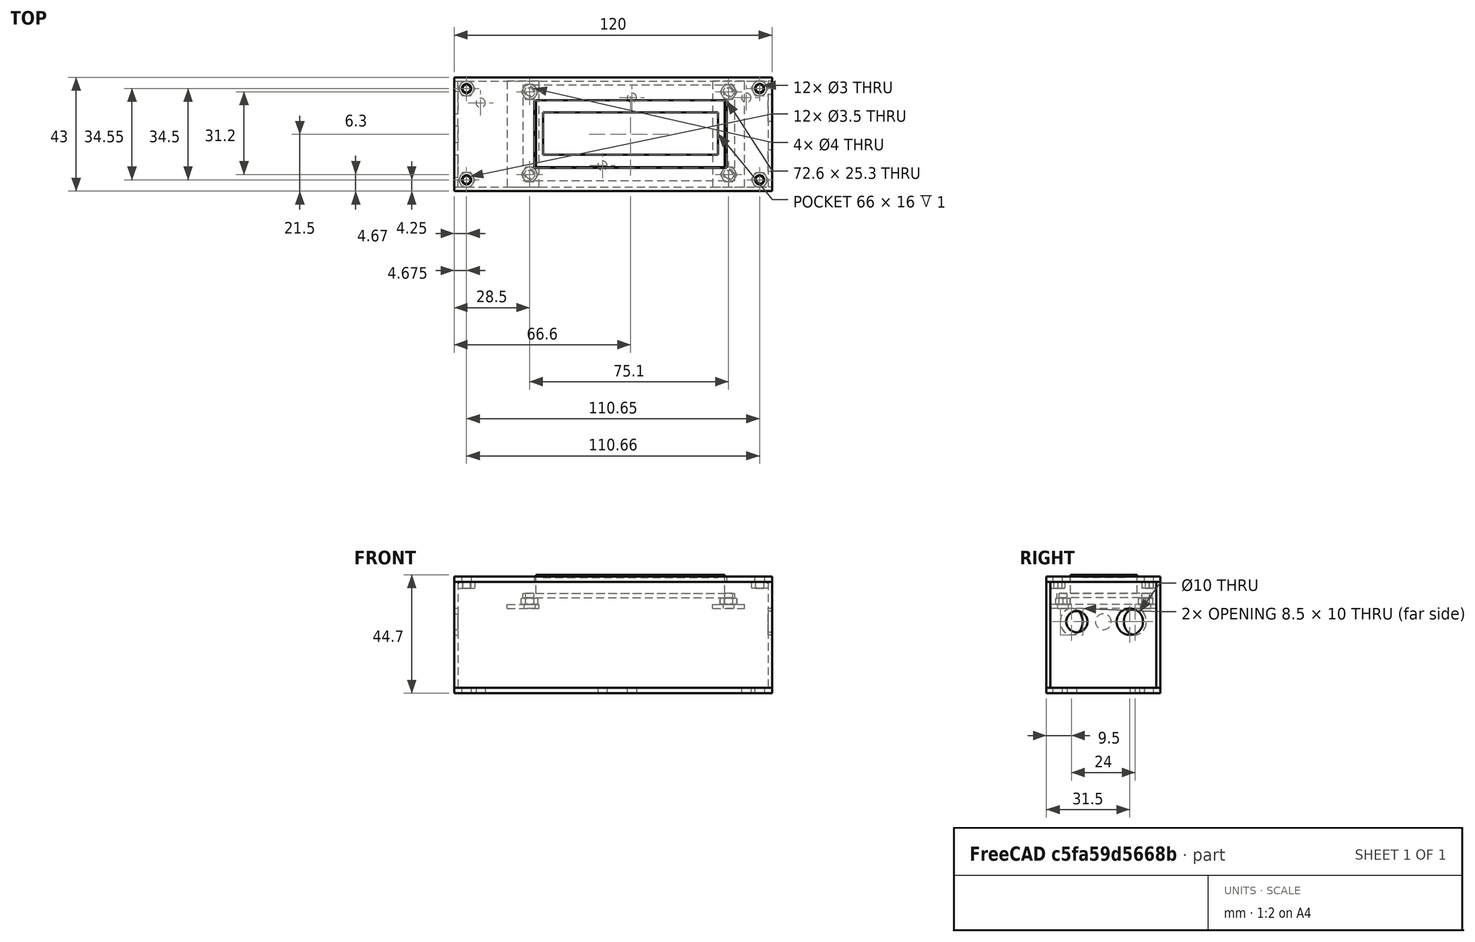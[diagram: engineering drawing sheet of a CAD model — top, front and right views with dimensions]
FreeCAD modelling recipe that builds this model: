
FCSTD DOCUMENT  (FreeCAD 0.19R24291 (Git))
Label: lc_meter_frame
License: All rights reserved
LicenseURL: http://en.wikipedia.org/wiki/All_rights_reserved
objects: TechDraw::DrawViewDimension×49, Sketcher::SketchObject×40, PartDesign::Pad×15, PartDesign::Pocket×14, PartDesign::Body×14, TechDraw::DrawViewPart×9, PartDesign::Mirrored×7, Part::Mirroring×7, TechDraw::DrawViewAnnotation×6, PartDesign::Groove×5, TechDraw::DrawSVGTemplate×4, TechDraw::DrawPage×4, App::Part×3, PartDesign::Plane×2, TechDraw::DrawViewDimExtent×2, TechDraw::DrawViewSection×2, PartDesign::Hole×1, TechDraw::DrawViewBalloon×1
note: 140 computed .brp shape members not serialized (recipe doc carries the construction recipe); baked Part::Feature solids carry a one-line shape summary decoded from their .brp

FEATURE [Sketcher::SketchObject] Sketch007
  FullyConstrained = true
  MapMode = 5
  Support = -> [XY_Plane006]
  sketch-geometry (7):
    g0: LineSegment StartX=1.58771 StartY=2.75 StartZ=0 EndX=-1.58771 EndY=2.75 EndZ=0
    g1: LineSegment StartX=-1.58771 StartY=2.75 StartZ=0 EndX=-3.17543 EndY=1.48956e-11 EndZ=0
    g2: LineSegment StartX=-3.17543 StartY=1.48956e-11 StartZ=0 EndX=-1.58771 EndY=-2.75 EndZ=0
    g3: LineSegment StartX=-1.58771 StartY=-2.75 StartZ=0 EndX=1.58771 EndY=-2.75 EndZ=0
    g4: LineSegment StartX=1.58771 StartY=-2.75 StartZ=0 EndX=3.17543 EndY=2.08953e-11 EndZ=0
    g5: LineSegment StartX=3.17543 StartY=2.08953e-11 StartZ=0 EndX=1.58771 EndY=2.75 EndZ=0
    g6: Circle CenterX=0 CenterY=0 CenterZ=0 NormalX=0 NormalY=0 NormalZ=1 AngleXU=0 Radius=3.17543
  constraints (16):
    c: Coincident(g0,g1)
    c: Coincident(g1,g2)
    c: Coincident(g2,g3)
    c: Coincident(g3,g4)
    c: Coincident(g4,g5)
    c: Coincident(g5,g0)
    c: Equal(g0, g1-g5) x5
    c: PointOnObject(g0,g6)
    c: PointOnObject(g1,g6)
    c: PointOnObject(g2,g6)
    c: PointOnObject(g3,g6)
    c: PointOnObject(g4,g6)
    c: PointOnObject(g5,g6)
    c: Coincident(g6,g-1)
    c: Horizontal(g0)
    c: Distance(g0,g3) = 5.5
FEATURE [PartDesign::Pad] Pad005
  Direction = (1,1,1)
  Length = 1.2
  Length2 = 1.2
  Profile = -> Sketch007
  Type = 4
FEATURE [Sketcher::SketchObject] Sketch008
  FullyConstrained = true
  MapMode = 5
  Placement = pos=(0,0,1.2) rot=(0,0,1;0rad)
  Support = -> [Pad005]
  sketch-geometry (1):
    g0: Circle CenterX=0 CenterY=0 CenterZ=0 NormalX=0 NormalY=0 NormalZ=1 AngleXU=0 Radius=1.5
  constraints (2):
    c: Coincident(g0,g-1)
    c: Diameter(g0) = 3
FEATURE [PartDesign::Pocket] Pocket002
  BaseFeature = -> Pad005
  Length = 5
  Length2 = 100
  Profile = -> Sketch008
  Type = 1
FEATURE [Sketcher::SketchObject] Sketch009
  ExternalGeometry = -> [Pocket002]
  FullyConstrained = true
  MapMode = 5
  Placement = pos=(0,2.75,0) rot=(0,0.707107,0.707107;3.14159rad)
  Support = -> [Pocket002]
  sketch-geometry (3):
    g0: LineSegment StartX=2.5 StartY=1.2 StartZ=0 EndX=3.17543 EndY=0.810042 EndZ=0
    g1: LineSegment StartX=3.17543 StartY=0.810042 StartZ=0 EndX=3.17543 EndY=1.2 EndZ=0
    g2: LineSegment StartX=3.17543 StartY=1.2 StartZ=0 EndX=2.5 EndY=1.2 EndZ=0
  constraints (7):
    c: Coincident(g0,g1)
    c: Coincident(g1,g2)
    c: Coincident(g2,g0)
    c: Tangent(g2,g-5)
    c: Tangent(g1,g-4)
    c: DistanceX(g-2,g0) = 2.5
    c: Angle(g0,g2) = 0.523599
FEATURE [Sketcher::SketchObject] Sketch010
  ExternalGeometry = -> [Pad005]
  FullyConstrained = true
  MapMode = 5
  Placement = pos=(0,0,0) rot=(1,0,0;1.5708rad)
  Support = -> [XZ_Plane006]
  sketch-geometry (3):
    g0: LineSegment StartX=-3.17543 StartY=1.2 StartZ=0 EndX=-3.17543 EndY=0.95438 EndZ=0
    g1: LineSegment StartX=-3.17543 StartY=0.95438 StartZ=0 EndX=-2.75 EndY=1.2 EndZ=0
    g2: LineSegment StartX=-2.75 StartY=1.2 StartZ=0 EndX=-3.17543 EndY=1.2 EndZ=0
  constraints (8):
    c: Coincident(g-4,g0)
    c: PointOnObject(g0,g-4)
    c: Coincident(g0,g1)
    c: PointOnObject(g1,g-3)
    c: Coincident(g1,g2)
    c: Coincident(g2,g0)
    c: Distance(g1,g-2) = 2.75
    c: Angle(g2,g1) = 0.523599
FEATURE [PartDesign::Groove] Groove
  Angle = 360
  Axis = (0,2e-16,1)
  Base = (0,0,0)
  BaseFeature = -> Pocket002
  Profile = -> Sketch010
  ReferenceAxis = -> Sketch010 [V_Axis]
  Reversed = true
FEATURE [PartDesign::Mirrored] Mirrored
  BaseFeature = -> Groove
  MirrorPlane = -> Sketch010 [H_Axis]
  Originals = -> [Groove]
FEATURE [PartDesign::Body] Body005  label="Screw M3 001"
  Group = -> [Sketch007,Pad005,Sketch008,Pocket002,Sketch009,Sketch010,Groove,Mirrored]
  Origin = -> Origin006
  Placement = pos=(4.675,8.25,3.2) rot=(0,0,1;0rad)
  Tip = -> Mirrored
FEATURE [Sketcher::SketchObject] Sketch005
  FullyConstrained = true
  MapMode = 5
  Support = -> [XY_Plane003]
  sketch-geometry (4):
    g0: LineSegment StartX=0 StartY=0 StartZ=0 EndX=120 EndY=0 EndZ=0
    g1: LineSegment StartX=120 StartY=0 StartZ=0 EndX=120 EndY=40 EndZ=0
    g2: LineSegment StartX=120 StartY=40 StartZ=0 EndX=0 EndY=40 EndZ=0
    g3: LineSegment StartX=0 StartY=40 StartZ=0 EndX=0 EndY=0 EndZ=0
  constraints (11):
    c: Coincident(g0,g1)
    c: Coincident(g1,g2)
    c: Coincident(g2,g3)
    c: Coincident(g3,g0)
    c: Horizontal(g0)
    c: Horizontal(g2)
    c: Vertical(g1)
    c: Vertical(g3)
    c: Coincident(g0,g-1)
    c: DistanceY(g1,g1) = 40
    c: DistanceX(g2,g2) = 120
FEATURE [PartDesign::Pad] Pad003
  Direction = (1,1,1)
  Length = 1.5
  Length2 = 100
  Profile = -> Sketch005
  Type = 0
FEATURE [PartDesign::Body] Body003  label="Side Panel 4"
  Group = -> [Sketch005,Pad003]
  Origin = -> Origin003
  Placement = pos=(0,5.5,2) rot=(1,0,0;1.5708rad)
  Tip = -> Pad003
FEATURE [Sketcher::SketchObject] Sketch003
  FullyConstrained = true
  MapMode = 5
  Support = -> [XY_Plane002]
  sketch-geometry (4):
    g0: LineSegment StartX=0 StartY=0 StartZ=0 EndX=40 EndY=0 EndZ=0
    g1: LineSegment StartX=40 StartY=0 StartZ=0 EndX=40 EndY=40 EndZ=0
    g2: LineSegment StartX=40 StartY=40 StartZ=0 EndX=0 EndY=40 EndZ=0
    g3: LineSegment StartX=0 StartY=40 StartZ=0 EndX=0 EndY=0 EndZ=0
  constraints (11):
    c: Coincident(g0,g1)
    c: Coincident(g1,g2)
    c: Coincident(g2,g3)
    c: Coincident(g3,g0)
    c: Horizontal(g0)
    c: Horizontal(g2)
    c: Vertical(g1)
    c: Vertical(g3)
    c: Coincident(g0,g-1)
    c: Equal(g2,g1)
    c: DistanceY(g1,g1) = 40
FEATURE [PartDesign::Pad] Pad002
  Direction = (1,1,1)
  Length = 1.5
  Length2 = 100
  Profile = -> Sketch003
  Type = 0
FEATURE [Sketcher::SketchObject] Sketch004
  ExternalGeometry = -> [Pad002]
  FullyConstrained = true
  MapMode = 5
  Placement = pos=(0,0,1.5) rot=(0,0,1;0rad)
  Support = -> [Pad002]
  sketch-geometry (9):
    g0: Ellipse CenterX=8 CenterY=25 CenterZ=0 NormalX=0 NormalY=0 NormalZ=1 MajorRadius=5 MinorRadius=4.25 AngleXU=1.5708
    g1: LineSegment StartX=8 StartY=30 StartZ=0 EndX=8 EndY=20 EndZ=0
    g2: LineSegment StartX=3.75 StartY=25 StartZ=0 EndX=12.25 EndY=25 EndZ=0
    g3: GeomPoint X=8 Y=27.6339 Z=0
    g4: GeomPoint X=8 Y=22.3661 Z=0
    g5: Circle CenterX=20 CenterY=25 CenterZ=0 NormalX=0 NormalY=0 NormalZ=1 AngleXU=0 Radius=3
    g6: Ellipse CenterX=32 CenterY=25 CenterZ=0 NormalX=0 NormalY=0 NormalZ=1 MajorRadius=5 MinorRadius=4.25 AngleXU=1.5708
    g7: LineSegment StartX=32 StartY=30 StartZ=0 EndX=32 EndY=20 EndZ=0
    g8: LineSegment StartX=27.75 StartY=25 StartZ=0 EndX=36.25 EndY=25 EndZ=0
  constraints (16):
    c: InternalAlignment(g1-g4 -> g0) x4
    c: InternalAlignment(g7,g6)
    c: InternalAlignment(g8,g6)
    c: Horizontal(g0,g5)
    c: Horizontal(g5,g6)
    c: Horizontal(g1,g7)
    c: Equal(g2,g8)
    c: Distance(g0,g-3) = 15
    c: Distance(g1,g1) = 10
    c: Vertical(g7)
    c: Vertical(g1)
    c: Distance(g2,g2) = 8.5
    c: Diameter(g5) = 6
    c: Distance(g6,g-5) = 8
    c: Distance(g0,g-4) = 8
    c: Distance(g5,g-5) = 20
FEATURE [PartDesign::Pocket] Pocket001
  BaseFeature = -> Pad002
  Length = 1.5
  Length2 = 100
  Profile = -> Sketch004
  Type = 0
FEATURE [PartDesign::Body] Body002  label="Side Panel 3"
  Group = -> [Sketch003,Pad002,Sketch004,Pocket001]
  Origin = -> Origin002
  Placement = pos=(0,5.5,2) rot=(0.57735,0.57735,0.57735;2.0944rad)
  Tip = -> Pocket001
FEATURE [Sketcher::SketchObject] Sketch
  FullyConstrained = true
  MapMode = 5
  Support = -> [XY_Plane]
  sketch-geometry (4):
    g0: LineSegment StartX=0 StartY=0 StartZ=0 EndX=120 EndY=0 EndZ=0
    g1: LineSegment StartX=120 StartY=0 StartZ=0 EndX=120 EndY=40 EndZ=0
    g2: LineSegment StartX=120 StartY=40 StartZ=0 EndX=0 EndY=40 EndZ=0
    g3: LineSegment StartX=0 StartY=40 StartZ=0 EndX=0 EndY=0 EndZ=0
  constraints (11):
    c: Coincident(g0,g1)
    c: Coincident(g1,g2)
    c: Coincident(g2,g3)
    c: Coincident(g3,g0)
    c: Horizontal(g0)
    c: Horizontal(g2)
    c: Vertical(g1)
    c: Vertical(g3)
    c: Coincident(g0,g-1)
    c: DistanceY(g1,g1) = 40
    c: DistanceX(g2,g2) = 120
FEATURE [PartDesign::Pad] Pad
  Direction = (1,1,1)
  Length = 1.5
  Length2 = 100
  Profile = -> Sketch
  Type = 0
FEATURE [PartDesign::Body] Body  label="Side Panel 1"
  Group = -> [Sketch,Pad]
  Origin = -> Origin
  Placement = pos=(0,47,2) rot=(1,0,0;1.5708rad)
  Tip = -> Pad
FEATURE [Sketcher::SketchObject] Sketch006
  FullyConstrained = true
  MapMode = 5
  Support = -> [XY_Plane005]
  sketch-geometry (4):
    g0: LineSegment StartX=0 StartY=0 StartZ=0 EndX=120 EndY=0 EndZ=0
    g1: LineSegment StartX=120 StartY=0 StartZ=0 EndX=120 EndY=43 EndZ=0
    g2: LineSegment StartX=120 StartY=43 StartZ=0 EndX=0 EndY=43 EndZ=0
    g3: LineSegment StartX=0 StartY=43 StartZ=0 EndX=0 EndY=0 EndZ=0
  constraints (11):
    c: Coincident(g0,g1)
    c: Coincident(g1,g2)
    c: Coincident(g2,g3)
    c: Coincident(g3,g0)
    c: Horizontal(g0)
    c: Horizontal(g2)
    c: Vertical(g1)
    c: Vertical(g3)
    c: Coincident(g0,g-1)
    c: DistanceY(g1,g1) = 43
    c: DistanceX(g2,g2) = 120
FEATURE [PartDesign::Pad] Pad004
  Direction = (1,1,1)
  Length = 2
  Length2 = 100
  Profile = -> Sketch006
  Type = 0
FEATURE [Sketcher::SketchObject] Sketch023
  ExternalGeometry = -> [Pad004]
  FullyConstrained = true
  MapMode = 5
  Placement = pos=(0,0,2) rot=(0,0,1;0rad)
  Support = -> [Pad004]
  sketch-geometry (2):
    g0: Circle CenterX=4.67 CenterY=38.75 CenterZ=0 NormalX=0 NormalY=0 NormalZ=1 AngleXU=0 Radius=1.75
    g1: Circle CenterX=115.33 CenterY=38.75 CenterZ=0 NormalX=0 NormalY=0 NormalZ=1 AngleXU=0 Radius=1.75
  constraints (6):
    c: Distance(g0,g-2) = 4.67
    c: Diameter(g0) = 3.5
    c: Distance(g0,g-3) = 4.25
    c: Diameter(g1) = 3.5
    c: Distance(g1,g-3) = 4.25
    c: Distance(g1,g-4) = 4.67
FEATURE [PartDesign::Pocket] Pocket003
  BaseFeature = -> Pad004
  Length = 5
  Length2 = 100
  Profile = -> Sketch023
  Type = 1
FEATURE [PartDesign::Plane] DatumPlane
  AttachmentOffset = pos=(0,21.5,0) rot=(1,0,0;1.5708rad)
  Length = 60
  MapMode = 5
  Placement = pos=(0,21.5,1.5) rot=(1,0,0;1.5708rad)
  ResizeMode = 0
  Width = 60
FEATURE [PartDesign::Mirrored] Mirrored001
  BaseFeature = -> Pocket003
  MirrorPlane = -> DatumPlane
  Originals = -> [Pocket003]
FEATURE [Part::Mirroring] Part__Mirroring  label="Screw M3 001 (Mirror #1)"
  Base = (60,0,0)
  Normal = (1,0,0)
  Source = -> Body005
FEATURE [Part::Mirroring] Part__Mirroring001  label="Screw M3 001 (Mirror #2)"
  Base = (0,27,0)
  Normal = (0,1,0)
  Placement = pos=(0,-3,0) rot=(0,0,1;0rad)
  Source = -> Body005
FEATURE [Part::Mirroring] Part__Mirroring002  label="Screw M3 001 (Mirror #3)"
  Base = (60,0,0)
  Normal = (1,0,0)
  Placement = pos=(0,0.05,0) rot=(0,0,1;0rad)
  Source = -> Part__Mirroring001
FEATURE [Part::Mirroring] Part__Mirroring003  label="Screw M3 001 (Mirror #4)"
  Base = (0,0,20)
  Normal = (0,0,1)
  Placement = pos=(0,0,4) rot=(0,0,1;0rad)
  Source = -> Body005
FEATURE [Part::Mirroring] Part__Mirroring004  label="Screw M3 001 (Mirror #5)"
  Base = (4.675,42.75,24)
  Normal = (0,0,1)
  Placement = pos=(0,0,-4) rot=(0,0,1;0rad)
  Source = -> Part__Mirroring001
FEATURE [Part::Mirroring] Part__Mirroring005  label="Screw M3 001 (Mirror #6)"
  Base = (0,0,22)
  Normal = (0,0,1)
  Source = -> Part__Mirroring002
FEATURE [Part::Mirroring] Part__Mirroring006  label="Screw M3 001 (Mirror #7)"
  Base = (0,0,22)
  Normal = (0,0,1)
  Source = -> Part__Mirroring
FEATURE [Sketcher::SketchObject] Sketch024
  FullyConstrained = true
  MapMode = 5
  Support = -> [XY_Plane009]
  sketch-geometry (4):
    g0: LineSegment StartX=0 StartY=0 StartZ=0 EndX=120 EndY=0 EndZ=0
    g1: LineSegment StartX=120 StartY=0 StartZ=0 EndX=120 EndY=43 EndZ=0
    g2: LineSegment StartX=120 StartY=43 StartZ=0 EndX=0 EndY=43 EndZ=0
    g3: LineSegment StartX=0 StartY=43 StartZ=0 EndX=0 EndY=0 EndZ=0
  constraints (11):
    c: Coincident(g0,g1)
    c: Coincident(g1,g2)
    c: Coincident(g2,g3)
    c: Coincident(g3,g0)
    c: Horizontal(g0)
    c: Horizontal(g2)
    c: Vertical(g1)
    c: Vertical(g3)
    c: Coincident(g0,g-1)
    c: DistanceY(g1,g1) = 43
    c: DistanceX(g2,g2) = 120
FEATURE [PartDesign::Pad] Pad006
  Direction = (1,1,1)
  Length = 2
  Length2 = 100
  Profile = -> Sketch024
  Type = 0
FEATURE [Sketcher::SketchObject] Sketch025
  ExternalGeometry = -> [Pad006]
  FullyConstrained = true
  MapMode = 5
  Placement = pos=(0,0,2) rot=(0,0,1;0rad)
  Support = -> [Pad006]
  sketch-geometry (2):
    g0: Circle CenterX=4.67 CenterY=38.75 CenterZ=0 NormalX=0 NormalY=0 NormalZ=1 AngleXU=0 Radius=1.75
    g1: Circle CenterX=115.33 CenterY=38.75 CenterZ=0 NormalX=0 NormalY=0 NormalZ=1 AngleXU=0 Radius=1.75
  constraints (6):
    c: Distance(g0,g-2) = 4.67
    c: Diameter(g0) = 3.5
    c: Distance(g0,g-3) = 4.25
    c: Diameter(g1) = 3.5
    c: Distance(g1,g-3) = 4.25
    c: Distance(g1,g-4) = 4.67
FEATURE [PartDesign::Pocket] Pocket004
  BaseFeature = -> Pad006
  Length = 5
  Length2 = 100
  Profile = -> Sketch025
  Type = 1
FEATURE [PartDesign::Plane] DatumPlane001
  AttachmentOffset = pos=(0,21.5,0) rot=(1,0,0;1.5708rad)
  Length = 60
  MapMode = 5
  Placement = pos=(0,21.5,1.5) rot=(1,0,0;1.5708rad)
  ResizeMode = 0
  Width = 60
FEATURE [PartDesign::Mirrored] Mirrored002
  BaseFeature = -> Pocket004
  MirrorPlane = -> DatumPlane001
  Originals = -> [Pocket004]
FEATURE [Sketcher::SketchObject] Sketch026
  ExternalGeometry = -> [Mirrored002]
  FullyConstrained = true
  MapMode = 5
  Placement = pos=(0,0,2) rot=(0,0,1;0rad)
  Support = -> [Mirrored002]
  sketch-geometry (4):
    g0: LineSegment StartX=30.3 StartY=34.15 StartZ=0 EndX=102.9 EndY=34.15 EndZ=0
    g1: LineSegment StartX=102.9 StartY=34.15 StartZ=0 EndX=102.9 EndY=8.85 EndZ=0
    g2: LineSegment StartX=102.9 StartY=8.85 StartZ=0 EndX=30.3 EndY=8.85 EndZ=0
    g3: LineSegment StartX=30.3 StartY=8.85 StartZ=0 EndX=30.3 EndY=34.15 EndZ=0
  constraints (12):
    c: Coincident(g0,g1)
    c: Coincident(g1,g2)
    c: Coincident(g2,g3)
    c: Coincident(g3,g0)
    c: Horizontal(g0)
    c: Horizontal(g2)
    c: Vertical(g1)
    c: Vertical(g3)
    c: DistanceY(g1,g0) = 25.3
    c: DistanceX(g0,g0) = 72.6
    c: DistanceY(g-1,g2) = 8.85
    c: Distance(g1,g-4) = 17.1
FEATURE [PartDesign::Pocket] Pocket005
  BaseFeature = -> Mirrored002
  Length = 5
  Length2 = 100
  Profile = -> Sketch026
  Type = 1
FEATURE [PartDesign::Body] Body006  label="Top Panel"
  Group = -> [Sketch024,Pad006,Sketch025,Pocket004,DatumPlane001,Mirrored002,Sketch026,Pocket005]
  Origin = -> Origin009
  Placement = pos=(0,4,42) rot=(0,0,1;0rad)
  Tip = -> Pocket005
FEATURE [Sketcher::SketchObject] Sketch027
  FullyConstrained = true
  MapMode = 5
  Support = -> [XY_Plane010]
  sketch-geometry (4):
    g0: LineSegment StartX=0 StartY=0 StartZ=0 EndX=12 EndY=0 EndZ=0
    g1: LineSegment StartX=12 StartY=0 StartZ=0 EndX=12 EndY=40 EndZ=0
    g2: LineSegment StartX=12 StartY=40 StartZ=0 EndX=0 EndY=40 EndZ=0
    g3: LineSegment StartX=0 StartY=40 StartZ=0 EndX=0 EndY=0 EndZ=0
  constraints (11):
    c: Coincident(g0,g1)
    c: Coincident(g1,g2)
    c: Coincident(g2,g3)
    c: Coincident(g3,g0)
    c: Horizontal(g0)
    c: Horizontal(g2)
    c: Vertical(g1)
    c: Vertical(g3)
    c: Coincident(g0,g-1)
    c: DistanceY(g0,g1) = 40
    c: DistanceX(g2,g1) = 12
FEATURE [PartDesign::Pad] Pad007
  Direction = (1,1,1)
  Length = 1.5
  Length2 = 100
  Profile = -> Sketch027
  Type = 0
FEATURE [Sketcher::SketchObject] Sketch028
  ExternalGeometry = -> [Pad007]
  FullyConstrained = true
  MapMode = 5
  Placement = pos=(0,0,1.5) rot=(0,0,1;0rad)
  Support = -> [Pad007]
  sketch-geometry (2):
    g0: Circle CenterX=6 CenterY=36 CenterZ=0 NormalX=0 NormalY=0 NormalZ=1 AngleXU=0 Radius=2
    g1: Circle CenterX=6 CenterY=4.8 CenterZ=0 NormalX=0 NormalY=0 NormalZ=1 AngleXU=0 Radius=2
  constraints (6):
    c: Diameter(g0) = 4
    c: Diameter(g1) = 4
    c: Distance(g0,g-3) = 4
    c: Distance(g1,g-1) = 4.8
    c: Vertical(g0,g1)
    c: Distance(g0,g-2) = 6
FEATURE [PartDesign::Pocket] Pocket006
  BaseFeature = -> Pad007
  Length = 5
  Length2 = 100
  Profile = -> Sketch028
  Type = 1
FEATURE [PartDesign::Body] Body007
  Group = -> [Sketch027,Pad007,Sketch028,Pocket006]
  Origin = -> Origin010
  Placement = pos=(97.6,5.5,32.04) rot=(0,0,1;0rad)
  Tip = -> Pocket006
FEATURE [Sketcher::SketchObject] Sketch031
  FullyConstrained = true
  MapMode = 5
  Support = -> [XY_Plane012]
  sketch-geometry (4):
    g0: LineSegment StartX=0 StartY=0 StartZ=0 EndX=80 EndY=0 EndZ=0
    g1: LineSegment StartX=80 StartY=0 StartZ=0 EndX=80 EndY=36 EndZ=0
    g2: LineSegment StartX=80 StartY=36 StartZ=0 EndX=0 EndY=36 EndZ=0
    g3: LineSegment StartX=0 StartY=36 StartZ=0 EndX=0 EndY=0 EndZ=0
  constraints (11):
    c: Coincident(g0,g1)
    c: Coincident(g1,g2)
    c: Coincident(g2,g3)
    c: Coincident(g3,g0)
    c: Horizontal(g0)
    c: Horizontal(g2)
    c: Vertical(g1)
    c: Vertical(g3)
    c: Coincident(g0,g-1)
    c: DistanceX(g2,g1) = 80
    c: DistanceY(g0,g1) = 36
FEATURE [PartDesign::Pad] Pad009
  Direction = (1,1,1)
  Length = 1.7
  Length2 = 100
  Profile = -> Sketch031
  Type = 0
FEATURE [Sketcher::SketchObject] Sketch032
  ExternalGeometry = -> [Pad009]
  FullyConstrained = true
  MapMode = 5
  Placement = pos=(0,0,1.7) rot=(0,0,1;0rad)
  Support = -> [Pad009]
  sketch-geometry (4):
    g0: LineSegment StartX=4.95 StartY=30.3 StartZ=0 EndX=76.15 EndY=30.3 EndZ=0
    g1: LineSegment StartX=76.15 StartY=30.3 StartZ=0 EndX=76.15 EndY=5.1 EndZ=0
    g2: LineSegment StartX=76.15 StartY=5.1 StartZ=0 EndX=4.95 EndY=5.1 EndZ=0
    g3: LineSegment StartX=4.95 StartY=5.1 StartZ=0 EndX=4.95 EndY=30.3 EndZ=0
  constraints (12):
    c: Coincident(g0,g1)
    c: Coincident(g1,g2)
    c: Coincident(g2,g3)
    c: Coincident(g3,g0)
    c: Horizontal(g0)
    c: Horizontal(g2)
    c: Vertical(g1)
    c: Vertical(g3)
    c: DistanceY(g1,g0) = 25.2
    c: DistanceX(g0,g0) = 71.2
    c: Distance(g0,g-3) = 5.7
    c: Distance(g0,g-2) = 4.95
FEATURE [PartDesign::Pad] Pad010
  BaseFeature = -> Pad009
  Direction = (1,1,1)
  Length = 7
  Length2 = 100
  Profile = -> Sketch032
  Type = 0
FEATURE [Sketcher::SketchObject] Sketch033
  ExternalGeometry = -> [Pad010]
  FullyConstrained = false
  MapMode = 5
  Placement = pos=(0,0,1.7) rot=(0,0,1;0rad)
  Support = -> [Pad010]
  sketch-geometry (4):
    g0: Circle CenterX=2.5 CenterY=33.5 CenterZ=0 NormalX=0 NormalY=0 NormalZ=1 AngleXU=0 Radius=1.5
    g1: Circle CenterX=2.5 CenterY=2.28424 CenterZ=0 NormalX=0 NormalY=0 NormalZ=1 AngleXU=0 Radius=1.5
    g2: Circle CenterX=77.6 CenterY=33.5 CenterZ=0 NormalX=0 NormalY=0 NormalZ=1 AngleXU=0 Radius=1.5
    g3: Circle CenterX=77.6 CenterY=2.28424 CenterZ=0 NormalX=0 NormalY=0 NormalZ=1 AngleXU=0 Radius=1.5
  constraints (11):
    c: Distance(g2,g-4) = 2.4
    c: Distance(g0,g-2) = 2.5
    c: Distance(g0,g-3) = 2.5
    c: Horizontal(g0,g2)
    c: Horizontal(g1,g3)
    c: Vertical(g0,g1)
    c: Vertical(g2,g3)
    c: Equal(g0,g2)
    c: Equal(g1,g3)
    c: Equal(g0,g1)
    c: Diameter(g0) = 3
FEATURE [PartDesign::Pocket] Pocket008
  BaseFeature = -> Pad010
  Length = 5
  Length2 = 100
  Profile = -> Sketch033
  Type = 1
FEATURE [Sketcher::SketchObject] Sketch034
  ExternalGeometry = -> [Pocket008]
  FullyConstrained = true
  MapMode = 5
  Placement = pos=(0,0,8.7) rot=(0,0,1;0rad)
  Support = -> [Pocket008]
  sketch-geometry (4):
    g0: LineSegment StartX=7.55 StartY=25.7 StartZ=0 EndX=73.55 EndY=25.7 EndZ=0
    g1: LineSegment StartX=73.55 StartY=25.7 StartZ=0 EndX=73.55 EndY=9.7 EndZ=0
    g2: LineSegment StartX=73.55 StartY=9.7 StartZ=0 EndX=7.55 EndY=9.7 EndZ=0
    g3: LineSegment StartX=7.55 StartY=9.7 StartZ=0 EndX=7.55 EndY=25.7 EndZ=0
  constraints (12):
    c: Coincident(g0,g1)
    c: Coincident(g1,g2)
    c: Coincident(g2,g3)
    c: Coincident(g3,g0)
    c: Horizontal(g0)
    c: Horizontal(g2)
    c: Vertical(g1)
    c: Vertical(g3)
    c: DistanceX(g0,g0) = 66
    c: DistanceY(g1,g1) = 16
    c: Distance(g0,g-2) = 7.55
    c: Distance(g0,g-3) = 10.3
FEATURE [PartDesign::Pocket] Pocket009
  BaseFeature = -> Pocket008
  Length = 1
  Length2 = 100
  Profile = -> Sketch034
  Type = 0
FEATURE [PartDesign::Body] Body009  label="1602 LCD "
  Group = -> [Sketch031,Pad009,Sketch032,Pad010,Sketch033,Pocket008,Sketch034,Pocket009]
  Origin = -> Origin012
  Placement = pos=(26,8,36) rot=(0,0,1;0rad)
  Tip = -> Pocket009
FEATURE [Sketcher::SketchObject] Sketch036
  FullyConstrained = true
  MapMode = 5
  Support = -> [XY_Plane013]
  sketch-geometry (4):
    g0: LineSegment StartX=0 StartY=0 StartZ=0 EndX=12 EndY=0 EndZ=0
    g1: LineSegment StartX=12 StartY=0 StartZ=0 EndX=12 EndY=40 EndZ=0
    g2: LineSegment StartX=12 StartY=40 StartZ=0 EndX=0 EndY=40 EndZ=0
    g3: LineSegment StartX=0 StartY=40 StartZ=0 EndX=0 EndY=0 EndZ=0
  constraints (11):
    c: Coincident(g0,g1)
    c: Coincident(g1,g2)
    c: Coincident(g2,g3)
    c: Coincident(g3,g0)
    c: Horizontal(g0)
    c: Horizontal(g2)
    c: Vertical(g1)
    c: Vertical(g3)
    c: Coincident(g0,g-1)
    c: DistanceY(g0,g1) = 40
    c: DistanceX(g2,g1) = 12
FEATURE [PartDesign::Pad] Pad011
  Direction = (1,1,1)
  Length = 1.5
  Length2 = 100
  Profile = -> Sketch036
  Type = 0
FEATURE [Sketcher::SketchObject] Sketch035
  ExternalGeometry = -> [Pad011]
  FullyConstrained = true
  MapMode = 5
  Placement = pos=(0,0,1.5) rot=(0,0,1;0rad)
  Support = -> [Pad011]
  sketch-geometry (2):
    g0: Circle CenterX=8.5 CenterY=36 CenterZ=0 NormalX=0 NormalY=0 NormalZ=1 AngleXU=0 Radius=2
    g1: Circle CenterX=8.5 CenterY=4.8 CenterZ=0 NormalX=0 NormalY=0 NormalZ=1 AngleXU=0 Radius=2
  constraints (6):
    c: Diameter(g0) = 4
    c: Diameter(g1) = 4
    c: Distance(g0,g-3) = 4
    c: Distance(g1,g-1) = 4.8
    c: Vertical(g0,g1)
    c: Distance(g0,g-4) = 3.5
FEATURE [PartDesign::Pocket] Pocket010
  BaseFeature = -> Pad011
  Length = 5
  Length2 = 100
  Profile = -> Sketch035
  Type = 1
FEATURE [PartDesign::Body] Body010
  Group = -> [Sketch036,Pad011,Sketch035,Pocket010]
  Origin = -> Origin013
  Placement = pos=(20,5.5,32.04) rot=(0,0,1;0rad)
  Tip = -> Pocket010
FEATURE [Sketcher::SketchObject] Sketch037
  FullyConstrained = true
  MapMode = 5
  Support = -> [XY_Plane014]
  sketch-geometry (7):
    g0: LineSegment StartX=1.58771 StartY=2.75 StartZ=0 EndX=-1.58771 EndY=2.75 EndZ=0
    g1: LineSegment StartX=-1.58771 StartY=2.75 StartZ=0 EndX=-3.17543 EndY=1.48956e-11 EndZ=0
    g2: LineSegment StartX=-3.17543 StartY=1.48956e-11 StartZ=0 EndX=-1.58771 EndY=-2.75 EndZ=0
    g3: LineSegment StartX=-1.58771 StartY=-2.75 StartZ=0 EndX=1.58771 EndY=-2.75 EndZ=0
    g4: LineSegment StartX=1.58771 StartY=-2.75 StartZ=0 EndX=3.17543 EndY=2.08953e-11 EndZ=0
    g5: LineSegment StartX=3.17543 StartY=2.08953e-11 StartZ=0 EndX=1.58771 EndY=2.75 EndZ=0
    g6: Circle CenterX=0 CenterY=0 CenterZ=0 NormalX=0 NormalY=0 NormalZ=1 AngleXU=0 Radius=3.17543
  constraints (16):
    c: Coincident(g0,g1)
    c: Coincident(g1,g2)
    c: Coincident(g2,g3)
    c: Coincident(g3,g4)
    c: Coincident(g4,g5)
    c: Coincident(g5,g0)
    c: Equal(g0, g1-g5) x5
    c: PointOnObject(g0,g6)
    c: PointOnObject(g1,g6)
    c: PointOnObject(g2,g6)
    c: PointOnObject(g3,g6)
    c: PointOnObject(g4,g6)
    c: PointOnObject(g5,g6)
    c: Coincident(g6,g-1)
    c: Horizontal(g0)
    c: Distance(g0,g3) = 5.5
FEATURE [PartDesign::Pad] Pad012
  Direction = (1,1,1)
  Length = 1.2
  Length2 = 1.2
  Profile = -> Sketch037
  Type = 4
FEATURE [Sketcher::SketchObject] Sketch038
  FullyConstrained = true
  MapMode = 5
  Placement = pos=(0,0,1.2) rot=(0,0,1;0rad)
  Support = -> [Pad012]
  sketch-geometry (1):
    g0: Circle CenterX=0 CenterY=0 CenterZ=0 NormalX=0 NormalY=0 NormalZ=1 AngleXU=0 Radius=1.5
  constraints (2):
    c: Coincident(g0,g-1)
    c: Diameter(g0) = 3
FEATURE [Sketcher::SketchObject] Sketch040
  ExternalGeometry = -> [Pad012]
  FullyConstrained = true
  MapMode = 5
  Placement = pos=(0,0,0) rot=(1,0,0;1.5708rad)
  Support = -> [XZ_Plane014]
  sketch-geometry (3):
    g0: LineSegment StartX=-3.17543 StartY=1.2 StartZ=0 EndX=-3.17543 EndY=0.95438 EndZ=0
    g1: LineSegment StartX=-3.17543 StartY=0.95438 StartZ=0 EndX=-2.75 EndY=1.2 EndZ=0
    g2: LineSegment StartX=-2.75 StartY=1.2 StartZ=0 EndX=-3.17543 EndY=1.2 EndZ=0
  constraints (8):
    c: Coincident(g-4,g0)
    c: PointOnObject(g0,g-4)
    c: Coincident(g0,g1)
    c: PointOnObject(g1,g-3)
    c: Coincident(g1,g2)
    c: Coincident(g2,g0)
    c: Distance(g1,g-2) = 2.75
    c: Angle(g2,g1) = 0.523599
FEATURE [PartDesign::Pocket] Pocket011
  BaseFeature = -> Pad012
  Length = 5
  Length2 = 100
  Profile = -> Sketch038
  Type = 1
FEATURE [Sketcher::SketchObject] Sketch039
  ExternalGeometry = -> [Pocket011]
  FullyConstrained = true
  MapMode = 5
  Placement = pos=(0,2.75,0) rot=(0,0.707107,0.707107;3.14159rad)
  Support = -> [Pocket011]
  sketch-geometry (3):
    g0: LineSegment StartX=2.5 StartY=1.2 StartZ=0 EndX=3.17543 EndY=0.810042 EndZ=0
    g1: LineSegment StartX=3.17543 StartY=0.810042 StartZ=0 EndX=3.17543 EndY=1.2 EndZ=0
    g2: LineSegment StartX=3.17543 StartY=1.2 StartZ=0 EndX=2.5 EndY=1.2 EndZ=0
  constraints (7):
    c: Coincident(g0,g1)
    c: Coincident(g1,g2)
    c: Coincident(g2,g0)
    c: Tangent(g2,g-5)
    c: Tangent(g1,g-4)
    c: DistanceX(g-2,g0) = 2.5
    c: Angle(g0,g2) = 0.523599
FEATURE [PartDesign::Groove] Groove001
  Angle = 360
  Axis = (0,2e-16,1)
  Base = (0,0,0)
  BaseFeature = -> Pocket011
  Profile = -> Sketch040
  ReferenceAxis = -> Sketch040 [V_Axis]
  Reversed = true
FEATURE [PartDesign::Mirrored] Mirrored003
  BaseFeature = -> Groove001
  MirrorPlane = -> Sketch040 [H_Axis]
  Originals = -> [Groove001]
FEATURE [PartDesign::Body] Body011  label="Screw M3 002"
  Group = -> [Sketch037,Pad012,Sketch038,Pocket011,Sketch039,Sketch040,Groove001,Mirrored003]
  Origin = -> Origin014
  Placement = pos=(103.575,41.5,34.76) rot=(0,0,1;0rad)
  Tip = -> Mirrored003
FEATURE [Sketcher::SketchObject] Sketch041
  FullyConstrained = true
  MapMode = 5
  Support = -> [XY_Plane015]
  sketch-geometry (7):
    g0: LineSegment StartX=1.58771 StartY=2.75 StartZ=0 EndX=-1.58771 EndY=2.75 EndZ=0
    g1: LineSegment StartX=-1.58771 StartY=2.75 StartZ=0 EndX=-3.17543 EndY=1.48956e-11 EndZ=0
    g2: LineSegment StartX=-3.17543 StartY=1.48956e-11 StartZ=0 EndX=-1.58771 EndY=-2.75 EndZ=0
    g3: LineSegment StartX=-1.58771 StartY=-2.75 StartZ=0 EndX=1.58771 EndY=-2.75 EndZ=0
    g4: LineSegment StartX=1.58771 StartY=-2.75 StartZ=0 EndX=3.17543 EndY=2.08953e-11 EndZ=0
    g5: LineSegment StartX=3.17543 StartY=2.08953e-11 StartZ=0 EndX=1.58771 EndY=2.75 EndZ=0
    g6: Circle CenterX=0 CenterY=0 CenterZ=0 NormalX=0 NormalY=0 NormalZ=1 AngleXU=0 Radius=3.17543
  constraints (16):
    c: Coincident(g0,g1)
    c: Coincident(g1,g2)
    c: Coincident(g2,g3)
    c: Coincident(g3,g4)
    c: Coincident(g4,g5)
    c: Coincident(g5,g0)
    c: Equal(g0, g1-g5) x5
    c: PointOnObject(g0,g6)
    c: PointOnObject(g1,g6)
    c: PointOnObject(g2,g6)
    c: PointOnObject(g3,g6)
    c: PointOnObject(g4,g6)
    c: PointOnObject(g5,g6)
    c: Coincident(g6,g-1)
    c: Horizontal(g0)
    c: Distance(g0,g3) = 5.5
FEATURE [PartDesign::Pad] Pad013
  Direction = (1,1,1)
  Length = 1.2
  Length2 = 1.2
  Profile = -> Sketch041
  Type = 4
FEATURE [Sketcher::SketchObject] Sketch042
  FullyConstrained = true
  MapMode = 5
  Placement = pos=(0,0,1.2) rot=(0,0,1;0rad)
  Support = -> [Pad013]
  sketch-geometry (1):
    g0: Circle CenterX=0 CenterY=0 CenterZ=0 NormalX=0 NormalY=0 NormalZ=1 AngleXU=0 Radius=1.5
  constraints (2):
    c: Coincident(g0,g-1)
    c: Diameter(g0) = 3
FEATURE [PartDesign::Pocket] Pocket012
  BaseFeature = -> Pad013
  Length = 5
  Length2 = 100
  Profile = -> Sketch042
  Type = 1
FEATURE [Sketcher::SketchObject] Sketch043
  ExternalGeometry = -> [Pocket012]
  FullyConstrained = true
  MapMode = 5
  Placement = pos=(0,2.75,0) rot=(0,0.707107,0.707107;3.14159rad)
  Support = -> [Pocket012]
  sketch-geometry (3):
    g0: LineSegment StartX=2.5 StartY=1.2 StartZ=0 EndX=3.17543 EndY=0.810042 EndZ=0
    g1: LineSegment StartX=3.17543 StartY=0.810042 StartZ=0 EndX=3.17543 EndY=1.2 EndZ=0
    g2: LineSegment StartX=3.17543 StartY=1.2 StartZ=0 EndX=2.5 EndY=1.2 EndZ=0
  constraints (7):
    c: Coincident(g0,g1)
    c: Coincident(g1,g2)
    c: Coincident(g2,g0)
    c: Tangent(g2,g-5)
    c: Tangent(g1,g-4)
    c: DistanceX(g-2,g0) = 2.5
    c: Angle(g0,g2) = 0.523599
FEATURE [Sketcher::SketchObject] Sketch044
  ExternalGeometry = -> [Pad013]
  FullyConstrained = true
  MapMode = 5
  Placement = pos=(0,0,0) rot=(1,0,0;1.5708rad)
  Support = -> [XZ_Plane015]
  sketch-geometry (3):
    g0: LineSegment StartX=-3.17543 StartY=1.2 StartZ=0 EndX=-3.17543 EndY=0.95438 EndZ=0
    g1: LineSegment StartX=-3.17543 StartY=0.95438 StartZ=0 EndX=-2.75 EndY=1.2 EndZ=0
    g2: LineSegment StartX=-2.75 StartY=1.2 StartZ=0 EndX=-3.17543 EndY=1.2 EndZ=0
  constraints (8):
    c: Coincident(g-4,g0)
    c: PointOnObject(g0,g-4)
    c: Coincident(g0,g1)
    c: PointOnObject(g1,g-3)
    c: Coincident(g1,g2)
    c: Coincident(g2,g0)
    c: Distance(g1,g-2) = 2.75
    c: Angle(g2,g1) = 0.523599
FEATURE [PartDesign::Groove] Groove002
  Angle = 360
  Axis = (0,2e-16,1)
  Base = (0,0,0)
  BaseFeature = -> Pocket012
  Profile = -> Sketch044
  ReferenceAxis = -> Sketch044 [V_Axis]
  Reversed = true
FEATURE [PartDesign::Mirrored] Mirrored004
  BaseFeature = -> Groove002
  MirrorPlane = -> Sketch044 [H_Axis]
  Originals = -> [Groove002]
FEATURE [PartDesign::Body] Body012  label="Screw M3 003"
  Group = -> [Sketch041,Pad013,Sketch042,Pocket012,Sketch043,Sketch044,Groove002,Mirrored004]
  Origin = -> Origin015
  Placement = pos=(103.625,10.3,34.75) rot=(0,0,1;0rad)
  Tip = -> Mirrored004
FEATURE [Sketcher::SketchObject] Sketch047
  FullyConstrained = true
  MapMode = 5
  Support = -> [XY_Plane016]
  sketch-geometry (7):
    g0: LineSegment StartX=1.58771 StartY=2.75 StartZ=0 EndX=-1.58771 EndY=2.75 EndZ=0
    g1: LineSegment StartX=-1.58771 StartY=2.75 StartZ=0 EndX=-3.17543 EndY=1.48956e-11 EndZ=0
    g2: LineSegment StartX=-3.17543 StartY=1.48956e-11 StartZ=0 EndX=-1.58771 EndY=-2.75 EndZ=0
    g3: LineSegment StartX=-1.58771 StartY=-2.75 StartZ=0 EndX=1.58771 EndY=-2.75 EndZ=0
    g4: LineSegment StartX=1.58771 StartY=-2.75 StartZ=0 EndX=3.17543 EndY=2.08953e-11 EndZ=0
    g5: LineSegment StartX=3.17543 StartY=2.08953e-11 StartZ=0 EndX=1.58771 EndY=2.75 EndZ=0
    g6: Circle CenterX=0 CenterY=0 CenterZ=0 NormalX=0 NormalY=0 NormalZ=1 AngleXU=0 Radius=3.17543
  constraints (16):
    c: Coincident(g0,g1)
    c: Coincident(g1,g2)
    c: Coincident(g2,g3)
    c: Coincident(g3,g4)
    c: Coincident(g4,g5)
    c: Coincident(g5,g0)
    c: Equal(g0, g1-g5) x5
    c: PointOnObject(g0,g6)
    c: PointOnObject(g1,g6)
    c: PointOnObject(g2,g6)
    c: PointOnObject(g3,g6)
    c: PointOnObject(g4,g6)
    c: PointOnObject(g5,g6)
    c: Coincident(g6,g-1)
    c: Horizontal(g0)
    c: Distance(g0,g3) = 5.5
FEATURE [PartDesign::Pad] Pad015
  Direction = (1,1,1)
  Length = 1.2
  Length2 = 1.2
  Profile = -> Sketch047
  Type = 4
FEATURE [Sketcher::SketchObject] Sketch048
  FullyConstrained = true
  MapMode = 5
  Placement = pos=(0,0,1.2) rot=(0,0,1;0rad)
  Support = -> [Pad015]
  sketch-geometry (1):
    g0: Circle CenterX=0 CenterY=0 CenterZ=0 NormalX=0 NormalY=0 NormalZ=1 AngleXU=0 Radius=1.5
  constraints (2):
    c: Coincident(g0,g-1)
    c: Diameter(g0) = 3
FEATURE [PartDesign::Pocket] Pocket013
  BaseFeature = -> Pad015
  Length = 5
  Length2 = 100
  Profile = -> Sketch048
  Type = 1
FEATURE [Sketcher::SketchObject] Sketch049
  ExternalGeometry = -> [Pocket013]
  FullyConstrained = true
  MapMode = 5
  Placement = pos=(0,2.75,0) rot=(0,0.707107,0.707107;3.14159rad)
  Support = -> [Pocket013]
  sketch-geometry (3):
    g0: LineSegment StartX=2.5 StartY=1.2 StartZ=0 EndX=3.17543 EndY=0.810042 EndZ=0
    g1: LineSegment StartX=3.17543 StartY=0.810042 StartZ=0 EndX=3.17543 EndY=1.2 EndZ=0
    g2: LineSegment StartX=3.17543 StartY=1.2 StartZ=0 EndX=2.5 EndY=1.2 EndZ=0
  constraints (7):
    c: Coincident(g0,g1)
    c: Coincident(g1,g2)
    c: Coincident(g2,g0)
    c: Tangent(g2,g-5)
    c: Tangent(g1,g-4)
    c: DistanceX(g-2,g0) = 2.5
    c: Angle(g0,g2) = 0.523599
FEATURE [Sketcher::SketchObject] Sketch050
  ExternalGeometry = -> [Pad015]
  FullyConstrained = true
  MapMode = 5
  Placement = pos=(0,0,0) rot=(1,0,0;1.5708rad)
  Support = -> [XZ_Plane016]
  sketch-geometry (3):
    g0: LineSegment StartX=-3.17543 StartY=1.2 StartZ=0 EndX=-3.17543 EndY=0.95438 EndZ=0
    g1: LineSegment StartX=-3.17543 StartY=0.95438 StartZ=0 EndX=-2.75 EndY=1.2 EndZ=0
    g2: LineSegment StartX=-2.75 StartY=1.2 StartZ=0 EndX=-3.17543 EndY=1.2 EndZ=0
  constraints (8):
    c: Coincident(g-4,g0)
    c: PointOnObject(g0,g-4)
    c: Coincident(g0,g1)
    c: PointOnObject(g1,g-3)
    c: Coincident(g1,g2)
    c: Coincident(g2,g0)
    c: Distance(g1,g-2) = 2.75
    c: Angle(g2,g1) = 0.523599
FEATURE [PartDesign::Groove] Groove004
  Angle = 360
  Axis = (0,2e-16,1)
  Base = (0,0,0)
  BaseFeature = -> Pocket013
  Profile = -> Sketch050
  ReferenceAxis = -> Sketch050 [V_Axis]
  Reversed = true
FEATURE [PartDesign::Mirrored] Mirrored005
  BaseFeature = -> Groove004
  MirrorPlane = -> Sketch050 [H_Axis]
  Originals = -> [Groove004]
FEATURE [PartDesign::Body] Body013  label="Screw M3 004"
  Group = -> [Sketch047,Pad015,Sketch048,Pocket013,Sketch049,Sketch050,Groove004,Mirrored005]
  Origin = -> Origin016
  Placement = pos=(28.51,41.5,34.75) rot=(0,0,1;0rad)
  Tip = -> Mirrored005
FEATURE [Sketcher::SketchObject] Sketch051
  FullyConstrained = true
  MapMode = 5
  Support = -> [XY_Plane017]
  sketch-geometry (7):
    g0: LineSegment StartX=1.58771 StartY=2.75 StartZ=0 EndX=-1.58771 EndY=2.75 EndZ=0
    g1: LineSegment StartX=-1.58771 StartY=2.75 StartZ=0 EndX=-3.17543 EndY=1.48956e-11 EndZ=0
    g2: LineSegment StartX=-3.17543 StartY=1.48956e-11 StartZ=0 EndX=-1.58771 EndY=-2.75 EndZ=0
    g3: LineSegment StartX=-1.58771 StartY=-2.75 StartZ=0 EndX=1.58771 EndY=-2.75 EndZ=0
    g4: LineSegment StartX=1.58771 StartY=-2.75 StartZ=0 EndX=3.17543 EndY=2.08953e-11 EndZ=0
    g5: LineSegment StartX=3.17543 StartY=2.08953e-11 StartZ=0 EndX=1.58771 EndY=2.75 EndZ=0
    g6: Circle CenterX=0 CenterY=0 CenterZ=0 NormalX=0 NormalY=0 NormalZ=1 AngleXU=0 Radius=3.17543
  constraints (16):
    c: Coincident(g0,g1)
    c: Coincident(g1,g2)
    c: Coincident(g2,g3)
    c: Coincident(g3,g4)
    c: Coincident(g4,g5)
    c: Coincident(g5,g0)
    c: Equal(g0, g1-g5) x5
    c: PointOnObject(g0,g6)
    c: PointOnObject(g1,g6)
    c: PointOnObject(g2,g6)
    c: PointOnObject(g3,g6)
    c: PointOnObject(g4,g6)
    c: PointOnObject(g5,g6)
    c: Coincident(g6,g-1)
    c: Horizontal(g0)
    c: Distance(g0,g3) = 5.5
FEATURE [PartDesign::Pad] Pad014
  Direction = (1,1,1)
  Length = 1.2
  Length2 = 1.2
  Profile = -> Sketch051
  Type = 4
FEATURE [Sketcher::SketchObject] Sketch046
  ExternalGeometry = -> [Pad014]
  FullyConstrained = true
  MapMode = 5
  Placement = pos=(0,0,0) rot=(1,0,0;1.5708rad)
  Support = -> [XZ_Plane017]
  sketch-geometry (3):
    g0: LineSegment StartX=-3.17543 StartY=1.2 StartZ=0 EndX=-3.17543 EndY=0.95438 EndZ=0
    g1: LineSegment StartX=-3.17543 StartY=0.95438 StartZ=0 EndX=-2.75 EndY=1.2 EndZ=0
    g2: LineSegment StartX=-2.75 StartY=1.2 StartZ=0 EndX=-3.17543 EndY=1.2 EndZ=0
  constraints (8):
    c: Coincident(g-4,g0)
    c: PointOnObject(g0,g-4)
    c: Coincident(g0,g1)
    c: PointOnObject(g1,g-3)
    c: Coincident(g1,g2)
    c: Coincident(g2,g0)
    c: Distance(g1,g-2) = 2.75
    c: Angle(g2,g1) = 0.523599
FEATURE [Sketcher::SketchObject] Sketch052
  FullyConstrained = true
  MapMode = 5
  Placement = pos=(0,0,1.2) rot=(0,0,1;0rad)
  Support = -> [Pad014]
  sketch-geometry (1):
    g0: Circle CenterX=0 CenterY=0 CenterZ=0 NormalX=0 NormalY=0 NormalZ=1 AngleXU=0 Radius=1.5
  constraints (2):
    c: Coincident(g0,g-1)
    c: Diameter(g0) = 3
FEATURE [PartDesign::Pocket] Pocket014
  BaseFeature = -> Pad014
  Length = 5
  Length2 = 100
  Profile = -> Sketch052
  Type = 1
FEATURE [PartDesign::Groove] Groove003
  Angle = 360
  Axis = (0,2e-16,1)
  Base = (0,0,0)
  BaseFeature = -> Pocket014
  Profile = -> Sketch046
  ReferenceAxis = -> Sketch046 [V_Axis]
  Reversed = true
FEATURE [PartDesign::Mirrored] Mirrored006
  BaseFeature = -> Groove003
  MirrorPlane = -> Sketch046 [H_Axis]
  Originals = -> [Groove003]
FEATURE [Sketcher::SketchObject] Sketch045
  ExternalGeometry = -> [Pocket014]
  FullyConstrained = true
  MapMode = 5
  Placement = pos=(0,2.75,0) rot=(0,0.707107,0.707107;3.14159rad)
  Support = -> [Pocket014]
  sketch-geometry (3):
    g0: LineSegment StartX=2.5 StartY=1.2 StartZ=0 EndX=3.17543 EndY=0.810042 EndZ=0
    g1: LineSegment StartX=3.17543 StartY=0.810042 StartZ=0 EndX=3.17543 EndY=1.2 EndZ=0
    g2: LineSegment StartX=3.17543 StartY=1.2 StartZ=0 EndX=2.5 EndY=1.2 EndZ=0
  constraints (7):
    c: Coincident(g0,g1)
    c: Coincident(g1,g2)
    c: Coincident(g2,g0)
    c: Tangent(g2,g-5)
    c: Tangent(g1,g-4)
    c: DistanceX(g-2,g0) = 2.5
    c: Angle(g0,g2) = 0.523599
FEATURE [PartDesign::Body] Body014  label="Screw M3 005"
  Group = -> [Sketch051,Pad014,Sketch052,Pocket014,Sketch045,Sketch046,Groove003,Mirrored006]
  Origin = -> Origin017
  Placement = pos=(28.5,10.28,34.75) rot=(0,0,1;0rad)
  Tip = -> Mirrored006
FEATURE [App::Part] Part001  label="Screws"
  Group = -> [Body005,Part__Mirroring001,Part__Mirroring002,Part__Mirroring,Part__Mirroring004,Part__Mirroring005,Part__Mirroring006,Part__Mirroring003,Body011,Body012,Body013,Body014]
  Origin = -> Origin008
FEATURE [Sketcher::SketchObject] Sketch053
  ExternalGeometry = -> [Mirrored001]
  FullyConstrained = true
  MapMode = 5
  Placement = pos=(0,0,2) rot=(0,0,1;0rad)
  Support = -> [Mirrored001]
  sketch-geometry (12):
    g0: LineSegment StartX=6 StartY=37.35 StartZ=0 EndX=60 EndY=37.35 EndZ=0
    g1: LineSegment StartX=60 StartY=37.35 StartZ=0 EndX=60 EndY=5.65 EndZ=0
    g2: LineSegment StartX=60 StartY=5.65 StartZ=0 EndX=6 EndY=5.65 EndZ=0
    g3: LineSegment StartX=6 StartY=5.65 StartZ=0 EndX=6 EndY=37.35 EndZ=0
    g4: LineSegment StartX=63.4 StartY=39 StartZ=0 EndX=114 EndY=39 EndZ=0
    g5: LineSegment StartX=114 StartY=39 StartZ=0 EndX=114 EndY=4 EndZ=0
    g6: LineSegment StartX=114 StartY=4 StartZ=0 EndX=63.4 EndY=4 EndZ=0
    g7: LineSegment StartX=63.4 StartY=4 StartZ=0 EndX=63.4 EndY=39 EndZ=0
    g8: Circle CenterX=67.1 CenterY=35.3 CenterZ=0 NormalX=0 NormalY=0 NormalZ=1 AngleXU=0 Radius=2
    g9: Circle CenterX=110.3 CenterY=35.3 CenterZ=0 NormalX=0 NormalY=0 NormalZ=1 AngleXU=0 Radius=2
    g10: Circle CenterX=56 CenterY=9.65 CenterZ=0 NormalX=0 NormalY=0 NormalZ=1 AngleXU=0 Radius=2
    g11: Circle CenterX=10 CenterY=33.35 CenterZ=0 NormalX=0 NormalY=0 NormalZ=1 AngleXU=0 Radius=2
  constraints (36):
    c: Coincident(g0,g1)
    c: Coincident(g1,g2)
    c: Coincident(g2,g3)
    c: Coincident(g3,g0)
    c: Horizontal(g0)
    c: Horizontal(g2)
    c: Vertical(g1)
    c: Vertical(g3)
    c: DistanceX(g0,g0) = 54
    c: DistanceY(g1,g1) = 31.7
    c: Coincident(g4,g5)
    c: Coincident(g5,g6)
    c: Coincident(g6,g7)
    c: Coincident(g7,g4)
    c: Horizontal(g4)
    c: Horizontal(g6)
    c: Vertical(g5)
    c: Vertical(g7)
    c: DistanceY(g5,g5) = 35
    c: DistanceX(g4,g4) = 50.6
    c: Horizontal(g8,g9)
    c: Distance(g9,g5) = 3.7
    c: Distance(g8,g7) = 3.7
    c: Diameter(g9) = 4
    c: Diameter(g8) = 4
    c: Diameter(g10) = 4
    c: Diameter(g11) = 4
    c: Distance(g8,g4) = 3.7
    c: Distance(g9,g-4) = 7.7
    c: Distance(g11,g0) = 4
    c: Distance(g11,g3) = 4
    c: Distance(g10,g2) = 4
    c: Distance(g10,g1) = 4
    c: Distance(g0,g-4) = 5.65
    c: Distance(g4,g-5) = 6
    c: Distance(g0,g-2) = 6
FEATURE [PartDesign::Hole] Hole
  BaseFeature = -> Mirrored001
  Depth = 25
  DepthType = 1
  Diameter = 3.5
  DrillForDepth = false
  DrillPoint = 1
  DrillPointAngle = 118
  HoleCutCountersinkAngle = 90
  HoleCutCustomValues = false
  HoleCutDepth = 0
  HoleCutDiameter = 6.1
  HoleCutType = 0
  ModelActualThread = false
  Profile = -> Sketch053
  Tapered = false
  TaperedAngle = 90
  ThreadAngle = 0
  ThreadClass = 0
  ThreadCutOffInner = 0
  ThreadCutOffOuter = 0
  ThreadDirection = 0
  ThreadFit = 0
  ThreadPitch = 0
  ThreadSize = 0
  ThreadType = 0
  Threaded = false
FEATURE [PartDesign::Body] Body004  label="Bottom Panel"
  Group = -> [Sketch006,Pad004,Sketch023,Pocket003,DatumPlane,Mirrored001,Sketch053,Hole]
  Origin = -> Origin005
  Placement = pos=(0,4,0) rot=(0,0,1;0rad)
  Tip = -> Hole
FEATURE [TechDraw::DrawSVGTemplate] Template001  label="T001"
  EditableTexts = AUTHOR_NAME=_edKotinsky; DN=1; DRAWING_TITLE=LC meter frame; FC-DATE=01/12/2021; FC-REV=REV A; FC-SC=1; FC-SH=1 / 4; FC-SI=A4; PN=1; SI-1=Top panel is plastic 2 mm
  Height = 210
  Orientation = 1
  Width = 297
FEATURE [Sketcher::SketchObject] Sketch001
  FullyConstrained = true
  MapMode = 5
  Support = -> [XY_Plane001]
  sketch-geometry (4):
    g0: LineSegment StartX=0 StartY=0 StartZ=0 EndX=40 EndY=0 EndZ=0
    g1: LineSegment StartX=40 StartY=0 StartZ=0 EndX=40 EndY=40 EndZ=0
    g2: LineSegment StartX=40 StartY=40 StartZ=0 EndX=0 EndY=40 EndZ=0
    g3: LineSegment StartX=0 StartY=40 StartZ=0 EndX=0 EndY=0 EndZ=0
  constraints (11):
    c: Coincident(g0,g1)
    c: Coincident(g1,g2)
    c: Coincident(g2,g3)
    c: Coincident(g3,g0)
    c: Horizontal(g0)
    c: Horizontal(g2)
    c: Vertical(g1)
    c: Vertical(g3)
    c: Coincident(g0,g-1)
    c: Equal(g2,g1)
    c: DistanceY(g1,g1) = 40
FEATURE [PartDesign::Pad] Pad001
  Direction = (1,1,1)
  Length = 1.5
  Length2 = 100
  Profile = -> Sketch001
  Type = 0
FEATURE [Sketcher::SketchObject] Sketch002
  ExternalGeometry = -> [Pad001]
  FullyConstrained = true
  MapMode = 5
  Placement = pos=(0,0,1.5) rot=(0,0,1;0rad)
  Support = -> [Pad001]
  sketch-geometry (2):
    g0: Circle CenterX=10 CenterY=25 CenterZ=0 NormalX=0 NormalY=0 NormalZ=1 AngleXU=0 Radius=5
    g1: Circle CenterX=30 CenterY=25 CenterZ=0 NormalX=0 NormalY=0 NormalZ=1 AngleXU=0 Radius=4
  constraints (6):
    c: Diameter(g0) = 10
    c: Diameter(g1) = 8
    c: Distance(g0,g-3) = 15
    c: Distance(g0,g-4) = 10
    c: Distance(g1,g-5) = 10
    c: Horizontal(g1,g0)
FEATURE [PartDesign::Pocket] Pocket
  BaseFeature = -> Pad001
  Length = 1.5
  Length2 = 100
  Profile = -> Sketch002
  Type = 0
FEATURE [PartDesign::Body] Body001  label="Side Panel 2"
  Group = -> [Sketch001,Pad001,Sketch002,Pocket]
  Origin = -> Origin001
  Placement = pos=(120,45.5,2) rot=(0.57735,-0.57735,-0.57735;2.0944rad)
  Tip = -> Pocket
FEATURE [App::Part] Part  label="Frame"
  Group = -> [Body001,Body003,Body002,Body,Body004,Body006,Body007,Body010]
  Origin = -> Origin004
FEATURE [TechDraw::DrawViewPart] View004
  CoarseView = false
  Direction = (0,0,1)
  Focus = 100
  HardHidden = false
  IsoCount = 0
  IsoHidden = false
  IsoVisible = false
  LockPosition = false
  Perspective = false
  Rotation = 0
  ScaleType = 0
  SeamHidden = false
  SeamVisible = true
  SmoothHidden = false
  SmoothVisible = true
  Source = -> [Body006]
  X = 138.908
  XDirection = (1,0,0)
  Y = 115.006
FEATURE [TechDraw::DrawViewDimension] Dimension003
  Arbitrary = false
  ArbitraryTolerances = false
  EqualTolerance = true
  FormatSpec = %.2f
  FormatSpecOverTolerance = %+.2f
  FormatSpecUnderTolerance = %+.2f
  Inverted = false
  LockPosition = false
  MeasureType = 1
  OverTolerance = 0
  References2D = -> [View004]
  Rotation = 0
  ScaleType = 0
  TheoreticalExact = false
  Type = 1
  UnderTolerance = 0
  X = -2.32211
  Y = 36.1602
FEATURE [TechDraw::DrawViewDimension] Dimension004
  Arbitrary = false
  ArbitraryTolerances = false
  EqualTolerance = true
  FormatSpec = %.2f
  FormatSpecOverTolerance = %+.2f
  FormatSpecUnderTolerance = %+.2f
  Inverted = false
  LockPosition = false
  MeasureType = 1
  OverTolerance = 0
  References2D = -> [View004]
  Rotation = 0
  ScaleType = 0
  TheoreticalExact = false
  Type = 2
  UnderTolerance = 0
  X = 68.8246
  Y = 1.10144
FEATURE [TechDraw::DrawSVGTemplate] Template
  EditableTexts = AUTHOR_NAME=_edKotinsky; DN=1; DRAWING_TITLE=LC meter frame; FC-DATE=02.12.2021; FC-REV=REV A; FC-SC=1; FC-SH=2 / 4; FC-SI=A4; FreeCAD_DRAWING=All 1.5 mm; PN=1; SI-1=Side and retaining panels are textolite
  Height = 210
  Orientation = 1
  Width = 297
FEATURE [TechDraw::DrawViewPart] View
  CoarseView = false
  Direction = (1,0,0)
  Focus = 100
  HardHidden = false
  IsoCount = 0
  IsoHidden = false
  IsoVisible = false
  LockPosition = false
  Perspective = false
  Rotation = 0
  ScaleType = 0
  SeamHidden = false
  SeamVisible = true
  SmoothHidden = false
  SmoothVisible = true
  Source = -> [Body001]
  X = 134.806
  XDirection = (0,1,0)
  Y = 125.615
FEATURE [TechDraw::DrawViewPart] View005
  CoarseView = false
  Direction = (1,0,0)
  Focus = 100
  HardHidden = false
  IsoCount = 0
  IsoHidden = false
  IsoVisible = false
  LockPosition = false
  Perspective = false
  Rotation = 0
  ScaleType = 0
  SeamHidden = false
  SeamVisible = true
  SmoothHidden = false
  SmoothVisible = true
  Source = -> [Body002]
  X = 59.3659
  XDirection = (0,1,0)
  Y = 109.498
FEATURE [TechDraw::DrawViewPart] View006
  CoarseView = false
  Direction = (0,0,1)
  Focus = 100
  HardHidden = false
  IsoCount = 0
  IsoHidden = false
  IsoVisible = false
  LockPosition = false
  Perspective = false
  Rotation = 0
  ScaleType = 0
  SeamHidden = false
  SeamVisible = true
  SmoothHidden = false
  SmoothVisible = true
  Source = -> [Body010]
  X = 195.536
  XDirection = (1,0,0)
  Y = 111.864
FEATURE [TechDraw::DrawViewPart] View007
  CoarseView = false
  Direction = (0,0,1)
  Focus = 100
  HardHidden = false
  IsoCount = 0
  IsoHidden = false
  IsoVisible = false
  LockPosition = false
  Perspective = false
  Rotation = 0
  ScaleType = 0
  SeamHidden = false
  SeamVisible = true
  SmoothHidden = false
  SmoothVisible = true
  Source = -> [Body007]
  X = 242.845
  XDirection = (1,0,0)
  Y = 133.237
FEATURE [TechDraw::DrawViewDimension] Dimension
  Arbitrary = false
  ArbitraryTolerances = false
  EqualTolerance = true
  FormatSpec = %.2f
  FormatSpecOverTolerance = %+.2f
  FormatSpecUnderTolerance = %+.2f
  Inverted = false
  LockPosition = false
  MeasureType = 1
  OverTolerance = 0
  References2D = -> [View004]
  Rotation = 0
  ScaleType = 0
  TheoreticalExact = false
  Type = 2
  UnderTolerance = 0
  X = 81.4305
  Y = 37.6843
FEATURE [TechDraw::DrawViewDimension] Dimension014
  Arbitrary = false
  ArbitraryTolerances = false
  EqualTolerance = true
  FormatSpec = %.2f
  FormatSpecOverTolerance = %+.2f
  FormatSpecUnderTolerance = %+.2f
  Inverted = false
  LockPosition = false
  MeasureType = 1
  OverTolerance = 0
  References2D = -> [View004]
  Rotation = 0
  ScaleType = 0
  TheoreticalExact = false
  Type = 1
  UnderTolerance = 0
  X = -70.3646
  Y = -37.0736
FEATURE [TechDraw::DrawViewDimension] Dimension015
  Arbitrary = false
  ArbitraryTolerances = false
  EqualTolerance = true
  FormatSpec = %.2f
  FormatSpecOverTolerance = %+.2f
  FormatSpecUnderTolerance = %+.2f
  Inverted = false
  LockPosition = false
  MeasureType = 1
  OverTolerance = 0
  References2D = -> [View004]
  Rotation = 0
  ScaleType = 0
  TheoreticalExact = false
  Type = 2
  UnderTolerance = 0
  X = -43.0355
  Y = 43.2513
FEATURE [TechDraw::DrawViewDimension] Dimension016
  Arbitrary = false
  ArbitraryTolerances = false
  EqualTolerance = true
  FormatSpec = %.2f
  FormatSpecOverTolerance = %+.2f
  FormatSpecUnderTolerance = %+.2f
  Inverted = false
  LockPosition = false
  MeasureType = 1
  OverTolerance = 0
  References2D = -> [View004]
  Rotation = 0
  ScaleType = 0
  TheoreticalExact = false
  Type = 1
  UnderTolerance = 0
  X = 5.02199
  Y = -37.0346
FEATURE [TechDraw::DrawViewDimension] Dimension017
  Arbitrary = false
  ArbitraryTolerances = false
  EqualTolerance = true
  FormatSpec = %.2f
  FormatSpecOverTolerance = %+.2f
  FormatSpecUnderTolerance = %+.2f
  Inverted = false
  LockPosition = false
  MeasureType = 1
  OverTolerance = 0
  References2D = -> [View004]
  Rotation = 0
  ScaleType = 0
  TheoreticalExact = false
  Type = 2
  UnderTolerance = 0
  X = -77.2727
  Y = 43.5688
FEATURE [TechDraw::DrawViewDimension] Dimension018
  Arbitrary = false
  ArbitraryTolerances = false
  EqualTolerance = true
  FormatSpec = %.2f
  FormatSpecOverTolerance = %+.2f
  FormatSpecUnderTolerance = %+.2f
  Inverted = false
  LockPosition = false
  MeasureType = 1
  OverTolerance = 0
  References2D = -> [View004]
  Rotation = 0
  ScaleType = 0
  TheoreticalExact = false
  Type = 1
  UnderTolerance = 0
  X = -73.7942
  Y = 0.800657
FEATURE [TechDraw::DrawViewDimension] Dimension019
  Arbitrary = false
  ArbitraryTolerances = false
  EqualTolerance = true
  FormatSpec = %.2f
  FormatSpecOverTolerance = %+.2f
  FormatSpecUnderTolerance = %+.2f
  Inverted = false
  LockPosition = false
  MeasureType = 1
  OverTolerance = 0
  References2D = -> [View]
  Rotation = 0
  ScaleType = 0
  TheoreticalExact = false
  Type = 2
  UnderTolerance = 0
  X = 27.8511
  Y = 1.39607
FEATURE [TechDraw::DrawViewDimension] Dimension020
  Arbitrary = false
  ArbitraryTolerances = false
  EqualTolerance = true
  FormatSpec = %.2f
  FormatSpecOverTolerance = %+.2f
  FormatSpecUnderTolerance = %+.2f
  Inverted = false
  LockPosition = false
  MeasureType = 1
  OverTolerance = 0
  References2D = -> [View]
  Rotation = 0
  ScaleType = 0
  TheoreticalExact = false
  Type = 1
  UnderTolerance = 0
  X = -1.17766
  Y = 33.1505
FEATURE [TechDraw::DrawViewDimension] Dimension021
  Arbitrary = false
  ArbitraryTolerances = false
  EqualTolerance = true
  FormatSpec = %.2f
  FormatSpecOverTolerance = %+.2f
  FormatSpecUnderTolerance = %+.2f
  Inverted = false
  LockPosition = false
  MeasureType = 1
  OverTolerance = 0
  References2D = -> [View]
  Rotation = 0
  ScaleType = 0
  TheoreticalExact = false
  Type = 1
  UnderTolerance = 0
  X = -29.7207
  Y = -22.7726
FEATURE [TechDraw::DrawViewDimension] Dimension022
  Arbitrary = false
  ArbitraryTolerances = false
  EqualTolerance = true
  FormatSpec = %.2f
  FormatSpecOverTolerance = %+.2f
  FormatSpecUnderTolerance = %+.2f
  Inverted = false
  LockPosition = false
  MeasureType = 1
  OverTolerance = 0
  References2D = -> [View]
  Rotation = 0
  ScaleType = 0
  TheoreticalExact = false
  Type = 1
  UnderTolerance = 0
  X = 31.0292
  Y = -22.7912
FEATURE [TechDraw::DrawViewDimension] Dimension023
  Arbitrary = false
  ArbitraryTolerances = false
  EqualTolerance = true
  FormatSpec = ⌀%.2f
  FormatSpecOverTolerance = %+.2f
  FormatSpecUnderTolerance = %+.2f
  Inverted = false
  LockPosition = false
  MeasureType = 1
  OverTolerance = 0
  References2D = -> [View004]
  Rotation = 0
  ScaleType = 0
  TheoreticalExact = false
  Type = 5
  UnderTolerance = 0
  X = -75
  Y = -11.5973
  expr: X = -75mm
FEATURE [TechDraw::DrawPage] Page001
  KeepUpdated = true
  NextBalloonIndex = 1
  ProjectionType = 0
  Template = -> Template001
  Views = -> [View004,Dimension003,Dimension004,Dimension,Dimension014,Dimension015,Dimension016,Dimension017,Dimension018,Dimension023]
FEATURE [TechDraw::DrawViewDimension] Dimension024
  Arbitrary = false
  ArbitraryTolerances = false
  EqualTolerance = true
  FormatSpec = ⌀%.2f
  FormatSpecOverTolerance = %+.2f
  FormatSpecUnderTolerance = %+.2f
  Inverted = false
  LockPosition = false
  MeasureType = 1
  OverTolerance = 0
  References2D = -> [View]
  Rotation = 0
  ScaleType = 0
  TheoreticalExact = false
  Type = 5
  UnderTolerance = 0
  X = -37.1746
  Y = 38.2303
FEATURE [TechDraw::DrawViewDimension] Dimension025
  Arbitrary = false
  ArbitraryTolerances = false
  EqualTolerance = true
  FormatSpec = ⌀%.2f
  FormatSpecOverTolerance = %+.2f
  FormatSpecUnderTolerance = %+.2f
  Inverted = false
  LockPosition = false
  MeasureType = 1
  OverTolerance = 0
  References2D = -> [View]
  Rotation = 0
  ScaleType = 0
  TheoreticalExact = false
  Type = 5
  UnderTolerance = 0
  X = -23.8316
  Y = 43.0002
FEATURE [TechDraw::DrawViewDimension] Dimension026
  Arbitrary = false
  ArbitraryTolerances = false
  EqualTolerance = true
  FormatSpec = %.2f
  FormatSpecOverTolerance = %+.2f
  FormatSpecUnderTolerance = %+.2f
  Inverted = false
  LockPosition = false
  MeasureType = 1
  OverTolerance = 0
  References2D = -> [View005]
  Rotation = 0
  ScaleType = 0
  TheoreticalExact = false
  Type = 2
  UnderTolerance = 0
  X = 28.2564
  Y = 3.09614
FEATURE [TechDraw::DrawViewDimension] Dimension027
  Arbitrary = false
  ArbitraryTolerances = false
  EqualTolerance = true
  FormatSpec = %.2f
  FormatSpecOverTolerance = %+.2f
  FormatSpecUnderTolerance = %+.2f
  Inverted = false
  LockPosition = false
  MeasureType = 1
  OverTolerance = 0
  References2D = -> [View005]
  Rotation = 0
  ScaleType = 0
  TheoreticalExact = false
  Type = 1
  UnderTolerance = 0
  X = -2.32211
  Y = 34.1907
FEATURE [TechDraw::DrawViewDimExtent] DimExtent
  Arbitrary = false
  ArbitraryTolerances = false
  CosmeticTags = cc2d3949-5127-47d8-b645-de22e9544c73 | 94c84f24-c3aa-40ee-8e5a-43b434f764fa
  DirExtent = 0
  EqualTolerance = true
  FormatSpec = %.2f
  FormatSpecOverTolerance = %+.2f
  FormatSpecUnderTolerance = %+.2f
  Inverted = false
  LockPosition = false
  MeasureType = 1
  OverTolerance = 0
  References2D = -> [View005]
  Rotation = 0
  ScaleType = 0
  Source = -> [View005]
  TheoreticalExact = false
  Type = 1
  UnderTolerance = 0
  X = -32.4755
  Y = -25.3831
FEATURE [TechDraw::DrawViewDimension] Dimension028
  Arbitrary = false
  ArbitraryTolerances = false
  EqualTolerance = true
  FormatSpec = %.2f
  FormatSpecOverTolerance = %+.2f
  FormatSpecUnderTolerance = %+.2f
  Inverted = false
  LockPosition = false
  MeasureType = 1
  OverTolerance = 0
  References2D = -> [View005]
  Rotation = 0
  ScaleType = 0
  TheoreticalExact = false
  Type = 1
  UnderTolerance = 0
  X = -32.7977
  Y = -35.7243
FEATURE [TechDraw::DrawViewDimension] Dimension029
  Arbitrary = false
  ArbitraryTolerances = false
  EqualTolerance = true
  FormatSpec = ⌀%.2f
  FormatSpecOverTolerance = %+.2f
  FormatSpecUnderTolerance = %+.2f
  Inverted = false
  LockPosition = false
  MeasureType = 1
  OverTolerance = 0
  References2D = -> [View005]
  Rotation = 0
  ScaleType = 0
  TheoreticalExact = false
  Type = 5
  UnderTolerance = 0
  X = 37.0793
  Y = -26.2541
FEATURE [TechDraw::DrawViewDimension] Dimension030
  Arbitrary = false
  ArbitraryTolerances = false
  EqualTolerance = true
  FormatSpec = %.2f
  FormatSpecOverTolerance = %+.2f
  FormatSpecUnderTolerance = %+.2f
  Inverted = false
  LockPosition = false
  MeasureType = 1
  OverTolerance = 0
  References2D = -> [View006]
  Rotation = 0
  ScaleType = 0
  TheoreticalExact = false
  Type = 1
  UnderTolerance = 0
  X = -14.4722
  Y = 46.793
FEATURE [TechDraw::DrawViewDimension] Dimension031
  Arbitrary = false
  ArbitraryTolerances = false
  EqualTolerance = true
  FormatSpec = %.2f
  FormatSpecOverTolerance = %+.2f
  FormatSpecUnderTolerance = %+.2f
  Inverted = false
  LockPosition = false
  MeasureType = 1
  OverTolerance = 0
  References2D = -> [View006]
  Rotation = 0
  ScaleType = 0
  TheoreticalExact = false
  Type = 2
  UnderTolerance = 0
  X = 12.4771
  Y = 1.57021
FEATURE [TechDraw::DrawViewDimension] Dimension032
  Arbitrary = false
  ArbitraryTolerances = false
  EqualTolerance = true
  FormatSpec = %.2f
  FormatSpecOverTolerance = %+.2f
  FormatSpecUnderTolerance = %+.2f
  Inverted = false
  LockPosition = false
  MeasureType = 1
  OverTolerance = 0
  References2D = -> [View006]
  Rotation = 0
  ScaleType = 0
  TheoreticalExact = false
  Type = 2
  UnderTolerance = 0
  X = -19.3723
  Y = 8.89194
FEATURE [TechDraw::DrawViewDimension] Dimension033
  Arbitrary = false
  ArbitraryTolerances = false
  EqualTolerance = true
  FormatSpec = %.2f
  FormatSpecOverTolerance = %+.2f
  FormatSpecUnderTolerance = %+.2f
  Inverted = false
  LockPosition = false
  MeasureType = 1
  OverTolerance = 0
  References2D = -> [View006]
  Rotation = 0
  ScaleType = 0
  TheoreticalExact = false
  Type = 1
  UnderTolerance = 0
  X = 17.4185
  Y = 35.9891
FEATURE [TechDraw::DrawViewDimension] Dimension034
  Arbitrary = false
  ArbitraryTolerances = false
  EqualTolerance = true
  FormatSpec = ⌀%.2f
  FormatSpecOverTolerance = %+.2f
  FormatSpecUnderTolerance = %+.2f
  Inverted = false
  LockPosition = false
  MeasureType = 1
  OverTolerance = 0
  References2D = -> [View006]
  Rotation = 0
  ScaleType = 0
  TheoreticalExact = false
  Type = 5
  UnderTolerance = 0
  X = 18.3654
  Y = -25.6817
FEATURE [TechDraw::DrawViewDimension] Dimension035
  Arbitrary = false
  ArbitraryTolerances = false
  EqualTolerance = true
  FormatSpec = %.2f
  FormatSpecOverTolerance = %+.2f
  FormatSpecUnderTolerance = %+.2f
  Inverted = false
  LockPosition = false
  MeasureType = 1
  OverTolerance = 0
  References2D = -> [View007]
  Rotation = 0
  ScaleType = 0
  TheoreticalExact = false
  Type = 1
  UnderTolerance = 0
  X = -0.681515
  Y = 36.3564
FEATURE [TechDraw::DrawViewDimension] Dimension036
  Arbitrary = false
  ArbitraryTolerances = false
  EqualTolerance = true
  FormatSpec = %.2f
  FormatSpecOverTolerance = %+.2f
  FormatSpecUnderTolerance = %+.2f
  Inverted = false
  LockPosition = false
  MeasureType = 1
  OverTolerance = 0
  References2D = -> [View007]
  Rotation = 0
  ScaleType = 0
  TheoreticalExact = false
  Type = 2
  UnderTolerance = 0
  X = 22.3564
  Y = 1.36303
FEATURE [TechDraw::DrawViewDimension] Dimension037
  Arbitrary = false
  ArbitraryTolerances = false
  EqualTolerance = true
  FormatSpec = %.2f
  FormatSpecOverTolerance = %+.2f
  FormatSpecUnderTolerance = %+.2f
  Inverted = false
  LockPosition = false
  MeasureType = 1
  OverTolerance = 0
  References2D = -> [View007]
  Rotation = 0
  ScaleType = 0
  TheoreticalExact = false
  Type = 2
  UnderTolerance = 0
  X = 12.8557
  Y = 8.32249
FEATURE [TechDraw::DrawViewDimension] Dimension038
  Arbitrary = false
  ArbitraryTolerances = false
  EqualTolerance = true
  FormatSpec = %.2f
  FormatSpecOverTolerance = %+.2f
  FormatSpecUnderTolerance = %+.2f
  Inverted = false
  LockPosition = false
  MeasureType = 1
  OverTolerance = 0
  References2D = -> [View007]
  Rotation = 0
  ScaleType = 0
  TheoreticalExact = false
  Type = 1
  UnderTolerance = 0
  X = -10.4017
  Y = -24.9771
FEATURE [TechDraw::DrawViewDimension] Dimension039
  Arbitrary = false
  ArbitraryTolerances = false
  EqualTolerance = true
  FormatSpec = ⌀%.2f
  FormatSpecOverTolerance = %+.2f
  FormatSpecUnderTolerance = %+.2f
  Inverted = false
  LockPosition = false
  MeasureType = 1
  OverTolerance = 0
  References2D = -> [View007]
  Rotation = 0
  ScaleType = 0
  TheoreticalExact = false
  Type = 5
  UnderTolerance = 0
  X = 22.6263
  Y = -31.486
FEATURE [TechDraw::DrawViewDimExtent] DimExtent001
  Arbitrary = false
  ArbitraryTolerances = false
  CosmeticTags = ed789e70-fde2-46dd-8066-f01223ff706a | 46c09f35-086f-42a2-b5fe-6000cda4a906
  DirExtent = 1
  EqualTolerance = true
  FormatSpec = %.2f
  FormatSpecOverTolerance = %+.2f
  FormatSpecUnderTolerance = %+.2f
  Inverted = false
  LockPosition = false
  MeasureType = 1
  OverTolerance = 0
  References2D = -> [View005]
  Rotation = 0
  ScaleType = 0
  Source = -> [View005]
  TheoreticalExact = false
  Type = 2
  UnderTolerance = 0
  X = -31.0771
  Y = 24.5345
FEATURE [TechDraw::DrawViewAnnotation] Annotation
  Font = osifont
  LineSpace = 80
  LockPosition = false
  MaxWidth = -1
  Rotation = 0
  ScaleType = 0
  Text = Side Panel with  | output terminals | and mode switch
  TextSize = 5
  TextStyle = 0
  X = 59.469
  Y = 50.7335
FEATURE [TechDraw::DrawViewAnnotation] Annotation001
  Font = osifont
  LineSpace = 80
  LockPosition = false
  MaxWidth = -1
  Rotation = 0
  ScaleType = 0
  Text = Side Panel with  | calibration btn | and power conn
  TextSize = 5
  TextStyle = 0
  X = 136.674
  Y = 78.1238
FEATURE [TechDraw::DrawViewAnnotation] Annotation002
  Font = osifont
  LineSpace = 80
  LockPosition = false
  MaxWidth = -1
  Rotation = 0
  ScaleType = 0
  Text = Display retaining panels
  TextSize = 5
  TextStyle = 0
  X = 218.312
  Y = 67.6912
FEATURE [TechDraw::DrawViewDimension] Dimension040
  Arbitrary = false
  ArbitraryTolerances = false
  EqualTolerance = true
  FormatSpec = %.2f
  FormatSpecOverTolerance = %+.2f
  FormatSpecUnderTolerance = %+.2f
  Inverted = false
  LockPosition = false
  MeasureType = 1
  OverTolerance = 0
  References2D = -> [View]
  Rotation = 0
  ScaleType = 0
  TheoreticalExact = false
  Type = 2
  UnderTolerance = 0
  X = -33.4872
  Y = -3.28062
FEATURE [TechDraw::DrawPage] Page  label="Page002"
  KeepUpdated = true
  NextBalloonIndex = 1
  ProjectionType = 0
  Template = -> Template
  Views = -> [View,View005,View006,View007,Dimension019,Dimension020,Dimension021,Dimension022,Dimension024,Dimension025,Dimension026,Dimension027,DimExtent,Dimension028,Dimension029,Dimension030,Dimension031,Dimension032,Dimension033,Dimension034,Dimension035,Dimension036,Dimension037,Dimension038,Dimension039,DimExtent001,Annotation,Annotation001,Annotation002,Dimension040]
FEATURE [TechDraw::DrawSVGTemplate] Template002
  EditableTexts = AUTHOR_NAME=_edKotinsky; DN=1; DRAWING_TITLE=LC meter frame; FC-DATE=02.12.2021; FC-REV=REV A; FC-SC=1; FC-SH=3 / 4; FC-SI=A4; FreeCAD_DRAWING=Bottom Panel is plastic 2 mm; PN=1; SI-1=Side Panels are 2 pieces; SI-3=Side Panels are textolite 1.5 mm
  Height = 210
  Orientation = 1
  Width = 297
FEATURE [TechDraw::DrawViewPart] View008
  CoarseView = false
  Direction = (0,-1,0)
  Focus = 100
  HardHidden = false
  IsoCount = 0
  IsoHidden = false
  IsoVisible = false
  LockPosition = false
  Perspective = false
  Rotation = 0
  ScaleType = 0
  SeamHidden = false
  SeamVisible = true
  SmoothHidden = false
  SmoothVisible = true
  Source = -> [Body003]
  X = 201.071
  XDirection = (1,0,0)
  Y = 155.197
FEATURE [TechDraw::DrawViewDimension] Dimension041
  Arbitrary = false
  ArbitraryTolerances = false
  EqualTolerance = true
  FormatSpec = %.2f
  FormatSpecOverTolerance = %+.2f
  FormatSpecUnderTolerance = %+.2f
  Inverted = false
  LockPosition = false
  MeasureType = 1
  OverTolerance = 0
  References2D = -> [View008]
  Rotation = 0
  ScaleType = 0
  TheoreticalExact = false
  Type = 2
  UnderTolerance = 0
  X = 65.1817
  Y = 1.17766
FEATURE [TechDraw::DrawViewDimension] Dimension042
  Arbitrary = false
  ArbitraryTolerances = false
  EqualTolerance = true
  FormatSpec = %.2f
  FormatSpecOverTolerance = %+.2f
  FormatSpecUnderTolerance = %+.2f
  Inverted = false
  LockPosition = false
  MeasureType = 1
  OverTolerance = 0
  References2D = -> [View008]
  Rotation = 0
  ScaleType = 0
  TheoreticalExact = false
  Type = 1
  UnderTolerance = 0
  X = 0.235532
  Y = 14.5828
FEATURE [TechDraw::DrawViewPart] View009
  CoarseView = false
  Direction = (0,0,-1)
  Focus = 100
  HardHidden = false
  IsoCount = 0
  IsoHidden = false
  IsoVisible = false
  LockPosition = false
  Perspective = false
  Rotation = 0
  ScaleType = 0
  SeamHidden = false
  SeamVisible = true
  SmoothHidden = false
  SmoothVisible = true
  Source = -> [Body004]
  X = 101.996
  XDirection = (1,0,0)
  Y = 95.3067
FEATURE [TechDraw::DrawViewDimension] Dimension043
  Arbitrary = false
  ArbitraryTolerances = false
  EqualTolerance = true
  FormatSpec = %.2f
  FormatSpecOverTolerance = %+.2f
  FormatSpecUnderTolerance = %+.2f
  Inverted = false
  LockPosition = false
  MeasureType = 1
  OverTolerance = 0
  References2D = -> [View009]
  Rotation = 0
  ScaleType = 0
  TheoreticalExact = false
  Type = 1
  UnderTolerance = 0
  X = -0.471063
  Y = 33.5121
FEATURE [TechDraw::DrawViewDimension] Dimension044
  Arbitrary = false
  ArbitraryTolerances = false
  EqualTolerance = true
  FormatSpec = %.2f
  FormatSpecOverTolerance = %+.2f
  FormatSpecUnderTolerance = %+.2f
  Inverted = false
  LockPosition = false
  MeasureType = 1
  OverTolerance = 0
  References2D = -> [View009]
  Rotation = 0
  ScaleType = 0
  TheoreticalExact = false
  Type = 2
  UnderTolerance = 0
  X = 74.4067
  Y = 1.60947
FEATURE [TechDraw::DrawViewDimension] Dimension045
  Arbitrary = false
  ArbitraryTolerances = false
  EqualTolerance = true
  FormatSpec = %.2f
  FormatSpecOverTolerance = %+.2f
  FormatSpecUnderTolerance = %+.2f
  Inverted = false
  LockPosition = false
  MeasureType = 1
  OverTolerance = 0
  References2D = -> [View009]
  Rotation = 0
  ScaleType = 0
  TheoreticalExact = false
  Type = 2
  UnderTolerance = 0
  X = -77.0465
  Y = 31.8177
FEATURE [TechDraw::DrawViewDimension] Dimension046
  Arbitrary = false
  ArbitraryTolerances = false
  EqualTolerance = true
  FormatSpec = %.2f
  FormatSpecOverTolerance = %+.2f
  FormatSpecUnderTolerance = %+.2f
  Inverted = false
  LockPosition = false
  MeasureType = 1
  OverTolerance = 0
  References2D = -> [View009]
  Rotation = 0
  ScaleType = 0
  TheoreticalExact = false
  Type = 1
  UnderTolerance = 0
  X = -60.0291
  Y = 39.9984
FEATURE [TechDraw::DrawViewDimension] Dimension047
  Arbitrary = false
  ArbitraryTolerances = false
  EqualTolerance = true
  FormatSpec = ⌀%.2f
  FormatSpecOverTolerance = %+.2f
  FormatSpecUnderTolerance = %+.2f
  Inverted = false
  LockPosition = false
  MeasureType = 1
  OverTolerance = 0
  References2D = -> [View009]
  Rotation = 0
  ScaleType = 0
  TheoreticalExact = false
  Type = 5
  UnderTolerance = 0
  X = -72.6745
  Y = -11.5858
FEATURE [TechDraw::DrawViewDimension] Dimension048
  Arbitrary = false
  ArbitraryTolerances = false
  EqualTolerance = true
  FormatSpec = %.2f
  FormatSpecOverTolerance = %+.2f
  FormatSpecUnderTolerance = %+.2f
  Inverted = false
  LockPosition = false
  MeasureType = 1
  OverTolerance = 0
  References2D = -> [View009]
  Rotation = 0
  ScaleType = 0
  TheoreticalExact = false
  Type = 1
  UnderTolerance = 0
  X = -69.5844
  Y = -25.3234
FEATURE [TechDraw::DrawViewDimension] Dimension049
  Arbitrary = false
  ArbitraryTolerances = false
  EqualTolerance = true
  FormatSpec = %.2f
  FormatSpecOverTolerance = %+.2f
  FormatSpecUnderTolerance = %+.2f
  Inverted = false
  LockPosition = false
  MeasureType = 1
  OverTolerance = 0
  References2D = -> [View009]
  Rotation = 0
  ScaleType = 0
  TheoreticalExact = false
  Type = 0
  UnderTolerance = 0
  X = -25.3487
  Y = -33.805
FEATURE [TechDraw::DrawViewDimension] Dimension050
  Arbitrary = false
  ArbitraryTolerances = false
  EqualTolerance = true
  FormatSpec = %.2f
  FormatSpecOverTolerance = %+.2f
  FormatSpecUnderTolerance = %+.2f
  Inverted = false
  LockPosition = false
  MeasureType = 1
  OverTolerance = 0
  References2D = -> [View009]
  Rotation = 0
  ScaleType = 0
  TheoreticalExact = false
  Type = 1
  UnderTolerance = 0
  X = 54.9341
  Y = -25.3651
FEATURE [TechDraw::DrawViewDimension] Dimension051
  Arbitrary = false
  ArbitraryTolerances = false
  EqualTolerance = true
  FormatSpec = %.2f
  FormatSpecOverTolerance = %+.2f
  FormatSpecUnderTolerance = %+.2f
  Inverted = false
  LockPosition = false
  MeasureType = 1
  OverTolerance = 0
  References2D = -> [View009]
  Rotation = 0
  ScaleType = 0
  TheoreticalExact = false
  Type = 1
  UnderTolerance = 0
  X = -35.5439
  Y = 9.82606
FEATURE [TechDraw::DrawViewDimension] Dimension052
  Arbitrary = false
  ArbitraryTolerances = false
  EqualTolerance = true
  FormatSpec = %.2f
  FormatSpecOverTolerance = %+.2f
  FormatSpecUnderTolerance = %+.2f
  Inverted = false
  LockPosition = false
  MeasureType = 1
  OverTolerance = 0
  References2D = -> [View009]
  Rotation = 0
  ScaleType = 0
  TheoreticalExact = false
  Type = 2
  UnderTolerance = 0
  X = 65.1584
  Y = -5.67714
FEATURE [TechDraw::DrawViewDimension] Dimension053
  Arbitrary = false
  ArbitraryTolerances = false
  EqualTolerance = true
  FormatSpec = %.2f
  FormatSpecOverTolerance = %+.2f
  FormatSpecUnderTolerance = %+.2f
  Inverted = false
  LockPosition = false
  MeasureType = 1
  OverTolerance = 0
  References2D = -> [View009]
  Rotation = 0
  ScaleType = 0
  TheoreticalExact = false
  Type = 2
  UnderTolerance = 0
  X = 8.91487
  Y = 7.05746
FEATURE [TechDraw::DrawViewDimension] Dimension054
  Arbitrary = false
  ArbitraryTolerances = false
  EqualTolerance = true
  FormatSpec = %.2f
  FormatSpecOverTolerance = %+.2f
  FormatSpecUnderTolerance = %+.2f
  Inverted = false
  LockPosition = false
  MeasureType = 1
  OverTolerance = 0
  References2D = -> [View009]
  Rotation = 0
  ScaleType = 0
  TheoreticalExact = false
  Type = 2
  UnderTolerance = 0
  X = -35.2859
  Y = -4.73485
FEATURE [TechDraw::DrawViewAnnotation] Annotation003
  Font = osifont
  LineSpace = 80
  LockPosition = false
  MaxWidth = -1
  Rotation = 0
  ScaleType = 0
  Text = Bottom Panel
  TextSize = 5
  TextStyle = 0
  X = 75.2246
  Y = 128.479
FEATURE [TechDraw::DrawViewAnnotation] Annotation004
  Font = osifont
  LineSpace = 80
  LockPosition = false
  MaxWidth = -1
  Rotation = 0
  ScaleType = 0
  Text = Side Panel
  TextSize = 5
  TextStyle = 0
  X = 202.941
  Y = 144.476
FEATURE [TechDraw::DrawSVGTemplate] Template003
  EditableTexts = AUTHOR_NAME=_edKotinsky; DN=1; DRAWING_TITLE=LC meter frame; FC-DATE=02.12.2021; FC-REV=REV A; FC-SC=0.8; FC-SH=4 / 4; FC-SI=A4; PN=1; SI-1=Common and internal view
  Height = 210
  Orientation = 1
  Width = 297
FEATURE [App::Part] Part002
  Group = -> [Part001,Part]
  Origin = -> Origin018
FEATURE [TechDraw::DrawViewPart] View010
  CoarseView = false
  Direction = (0,1,0)
  Focus = 100
  HardHidden = false
  IsoCount = 0
  IsoHidden = false
  IsoVisible = false
  LockPosition = false
  Perspective = false
  Rotation = 0
  Scale = 0.8
  ScaleType = 0
  SeamHidden = false
  SeamVisible = true
  SmoothHidden = false
  SmoothVisible = true
  Source = -> [Part002]
  X = 108.478
  XDirection = (-1,0,0)
  Y = 123.993
FEATURE [TechDraw::DrawViewSection] SectionView  label="Section  - "
  BaseView = -> View010
  CoarseView = false
  CutSurfaceDisplay = 2
  Direction = (-1,0,0)
  FileGeomPattern = <path>
  FileHatchPattern = <path>
  Focus = 100
  FuseBeforeCut = false
  HardHidden = false
  HatchScale = 1
  IsoCount = 0
  IsoHidden = false
  IsoVisible = false
  LockPosition = false
  NameGeomPattern = Diamond
  Perspective = false
  Rotation = 0
  Scale = 0.8
  ScaleType = 0
  SeamHidden = false
  SeamVisible = true
  SectionDirection = 1
  SectionNormal = (-1,0,0)
  SectionOrigin = (60,25.5,22)
  SmoothHidden = false
  SmoothVisible = true
  Source = -> [Part002]
  X = 66.0262
  XDirection = (0,-1,0)
  Y = 71.7372
FEATURE [TechDraw::DrawViewSection] SectionView001  label="Section  - 001"
  BaseView = -> View010
  CoarseView = false
  CutSurfaceDisplay = 2
  Direction = (0,0,-1)
  FileGeomPattern = <path>
  FileHatchPattern = <path>
  Focus = 100
  FuseBeforeCut = false
  HardHidden = false
  HatchScale = 1
  IsoCount = 0
  IsoHidden = false
  IsoVisible = false
  LockPosition = false
  NameGeomPattern = Diamond
  Perspective = false
  Rotation = 0
  Scale = 0.8
  ScaleType = 0
  SeamHidden = false
  SeamVisible = true
  SectionDirection = 2
  SectionNormal = (0,0,-1)
  SectionOrigin = (60,25.5,22)
  SmoothHidden = false
  SmoothVisible = true
  Source = -> [Part002]
  X = 86.4422
  XDirection = (1,0,0)
  Y = 140.345
FEATURE [TechDraw::DrawViewDimension] Dimension055
  Arbitrary = false
  ArbitraryTolerances = false
  EqualTolerance = true
  FormatSpec = %.2f
  FormatSpecOverTolerance = %+.2f
  FormatSpecUnderTolerance = %+.2f
  Inverted = false
  LockPosition = false
  MeasureType = 1
  OverTolerance = 0
  References2D = -> [SectionView]
  Rotation = 0
  ScaleType = 0
  TheoreticalExact = false
  Type = 0
  UnderTolerance = 0
  X = 31.0405
  Y = 2.00339
FEATURE [TechDraw::DrawViewDimension] Dimension056
  Arbitrary = false
  ArbitraryTolerances = false
  EqualTolerance = true
  FormatSpec = %.2f
  FormatSpecOverTolerance = %+.2f
  FormatSpecUnderTolerance = %+.2f
  Inverted = false
  LockPosition = false
  MeasureType = 1
  OverTolerance = 0
  References2D = -> [SectionView001]
  Rotation = 0
  ScaleType = 0
  TheoreticalExact = false
  Type = 1
  UnderTolerance = 0
  X = -40.4346
  Y = 29.4299
FEATURE [TechDraw::DrawViewDimension] Dimension057
  Arbitrary = false
  ArbitraryTolerances = false
  EqualTolerance = true
  FormatSpec = %.2f
  FormatSpecOverTolerance = %+.2f
  FormatSpecUnderTolerance = %+.2f
  Inverted = false
  LockPosition = false
  MeasureType = 1
  OverTolerance = 0
  References2D = -> [SectionView001]
  Rotation = 0
  ScaleType = 0
  TheoreticalExact = false
  Type = 1
  UnderTolerance = 0
  X = 32.3038
  Y = 29.5935
FEATURE [TechDraw::DrawViewPart] View011
  CoarseView = false
  Direction = (-0.577,0.577,0.577)
  Focus = 100
  HardHidden = false
  IsoCount = 0
  IsoHidden = false
  IsoVisible = false
  LockPosition = false
  Perspective = false
  Rotation = 0
  Scale = 0.8
  ScaleType = 0
  SeamHidden = false
  SeamVisible = true
  SmoothHidden = false
  SmoothVisible = true
  Source = -> [Part002]
  X = 209.649
  XDirection = (-0.707,-0.707,0)
  Y = 112.224
FEATURE [TechDraw::DrawViewBalloon] Balloon
  BubbleShape = 0
  EndType = 0
  EndTypeScale = 1
  KinkLength = 5
  LockPosition = false
  OriginX = -7.139
  OriginY = -71.7908
  Rotation = 0
  ScaleType = 0
  ShapeScale = 1
  SourceView = -> SectionView001
  Text = 1
  TextWrapLen = -1
  X = 4.42148
  Y = -44.6173
FEATURE [TechDraw::DrawViewAnnotation] Annotation005
  Font = osifont
  LineSpace = 80
  LockPosition = false
  MaxWidth = -1
  Rotation = 0
  ScaleType = 0
  Text = 1 Solder the screws to the  | copper layer of the textolite panels
  TextSize = 5
  TextStyle = 0
  X = 59.1864
  Y = 28.1225
FEATURE [TechDraw::DrawViewDimension] Dimension059
  Arbitrary = false
  ArbitraryTolerances = false
  EqualTolerance = true
  FormatSpec = %.2f
  FormatSpecOverTolerance = %+.2f
  FormatSpecUnderTolerance = %+.2f
  Inverted = false
  LockPosition = false
  MeasureType = 1
  OverTolerance = 0
  References2D = -> [SectionView001]
  Rotation = 0
  ScaleType = 0
  TheoreticalExact = false
  Type = 2
  UnderTolerance = 0
  X = -56.3145
  Y = -26.959
FEATURE [TechDraw::DrawPage] Page003  label="Page004"
  KeepUpdated = true
  NextBalloonIndex = 4
  ProjectionType = 0
  Template = -> Template003
  Views = -> [View010,SectionView,SectionView001,Dimension055,Dimension056,Dimension057,View011,Balloon,Annotation005,Dimension059]
FEATURE [TechDraw::DrawViewDimension] Dimension060
  Arbitrary = false
  ArbitraryTolerances = false
  EqualTolerance = true
  FormatSpec = %.2f
  FormatSpecOverTolerance = %+.2f
  FormatSpecUnderTolerance = %+.2f
  Inverted = false
  LockPosition = false
  MeasureType = 1
  OverTolerance = 0
  References2D = -> [View009]
  Rotation = 0
  ScaleType = 0
  TheoreticalExact = false
  Type = 1
  UnderTolerance = 0
  X = 27.9534
  Y = -25.3935
FEATURE [TechDraw::DrawPage] Page002  label="Page003"
  KeepUpdated = true
  NextBalloonIndex = 2
  ProjectionType = 0
  Template = -> Template002
  Views = -> [View008,View009,Dimension041,Dimension042,Dimension043,Dimension044,Dimension045,Dimension046,Dimension047,Dimension048,Dimension049,Dimension050,Dimension051,Dimension052,Dimension053,Dimension054,Annotation003,Annotation004,Dimension060]
note: 4 file-system paths scrubbed to <path> (originals preserved in the JSON sidecar)
